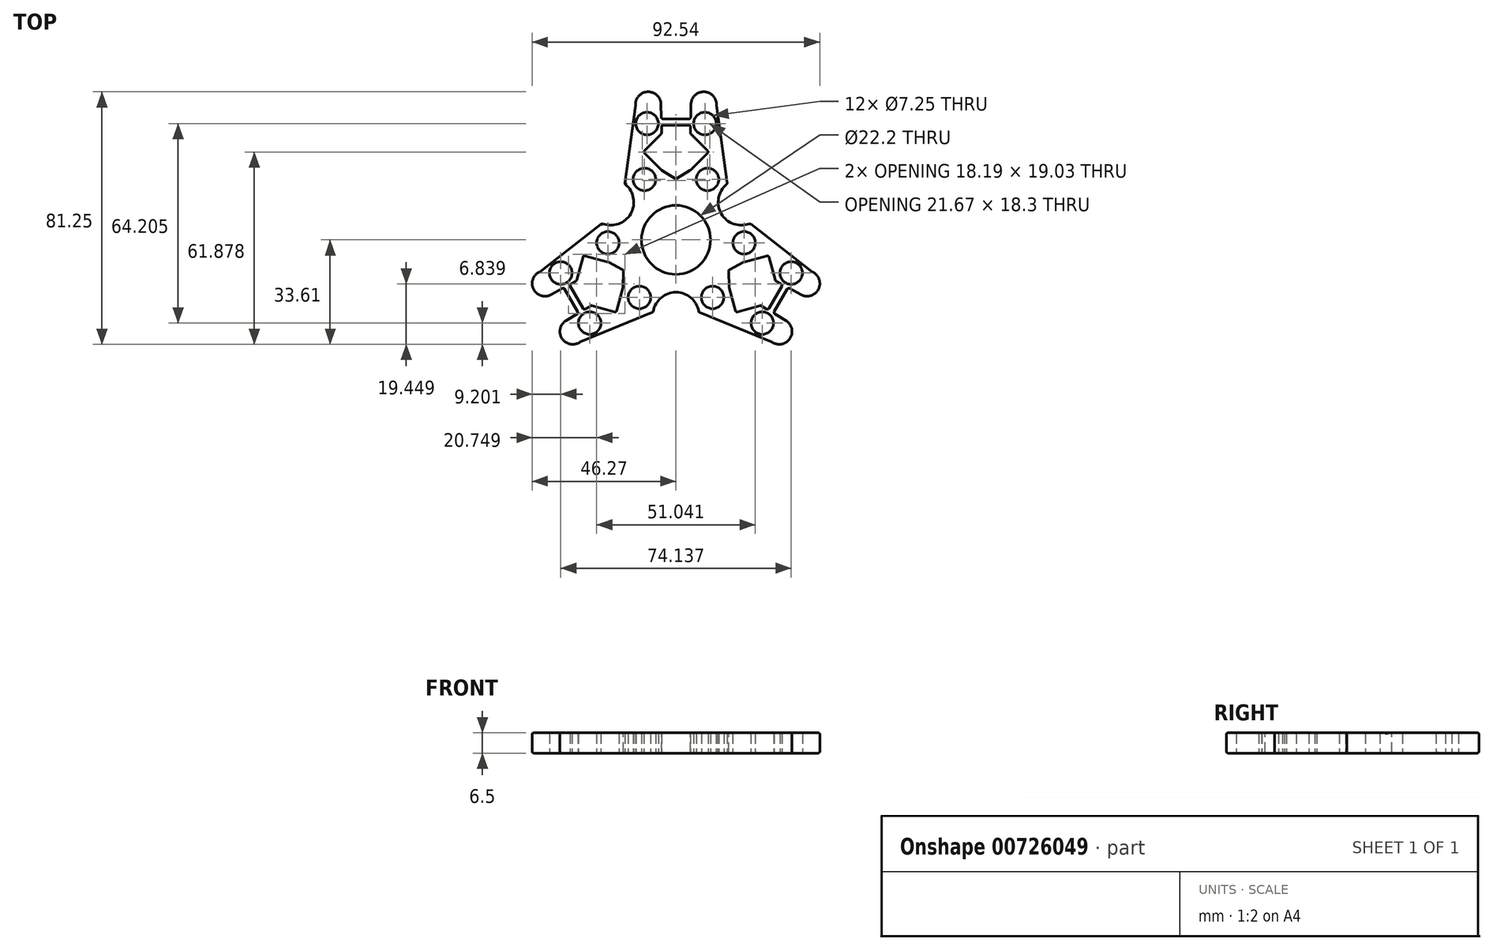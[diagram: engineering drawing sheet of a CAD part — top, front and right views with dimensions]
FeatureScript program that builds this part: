
annotation { "Feature Type Name" : "Feature", "Feature Type Description" : "" }
export const myFeature = defineFeature(function(context is Context, id is Id, definition is map)
    precondition{}
    {
        {
            var Q0;
            Q0=qCreatedBy(makeId("Top.planeOp"),FACE);
            var sketch = newSketch(context, id + "F0", { "sketchPlane" : qUnion([Q0])});
            skCircle(sketch, "E0", {"center": v(0, 0) * mm, "radius": 11.1 * mm});
            skCircle(sketch, "E1", {"center": v(0, 0) * mm, "radius": 14 * mm});
            skPoint(sketch, "E2", {"position": v(-16.47, 18) * mm});
            skPoint(sketch, "E3", {"position": v(-13.03, 43.23) * mm});
            skPoint(sketch, "E4.MirrorP", {"position": v(13.03, 43.23) * mm});
            skPoint(sketch, "E5.MirrorP", {"position": v(16.47, 18) * mm});
            skPoint(sketch, "E6", {"position": v(-4.8, 43.61) * mm});
            skPoint(sketch, "E7", {"position": v(-4.62, 34.25) * mm});
            skPoint(sketch, "E8", {"position": v(-10.54, 28.32) * mm});
            skPoint(sketch, "E9", {"position": v(-4.62, 22.4) * mm});
            skPoint(sketch, "E10", {"position": v(0, 19.53) * mm});
            skPoint(sketch, "E11.MirrorP", {"position": v(4.62, 22.4) * mm});
            skPoint(sketch, "E12.MirrorP", {"position": v(10.54, 28.32) * mm});
            skPoint(sketch, "E13.MirrorP", {"position": v(4.62, 34.25) * mm});
            skPoint(sketch, "E14.MirrorP", {"position": v(4.8, 43.61) * mm});
            skLineSegment(sketch, "E15", {"start": v(-16.47, 18) * mm, "end": v(-13.03, 43.23) * mm});
            skLineSegment(sketch, "E16", {"start": v(-13.03, 43.23) * mm, "end": v(-4.8, 43.61) * mm});
            skLineSegment(sketch, "E17", {"start": v(-4.8, 43.61) * mm, "end": v(-4.62, 34.25) * mm});
            skLineSegment(sketch, "E18", {"start": v(-10.54, 28.32) * mm, "end": v(-4.62, 34.25) * mm});
            skLineSegment(sketch, "E19", {"start": v(-10.54, 28.32) * mm, "end": v(-4.62, 22.4) * mm});
            skLineSegment(sketch, "E20", {"start": v(-4.62, 22.4) * mm, "end": v(0, 19.53) * mm});
            skLineSegment(sketch, "E21", {"start": v(0, 19.53) * mm, "end": v(4.62, 22.4) * mm});
            skLineSegment(sketch, "E22", {"start": v(4.62, 22.4) * mm, "end": v(10.54, 28.32) * mm});
            skLineSegment(sketch, "E23", {"start": v(4.62, 34.25) * mm, "end": v(10.54, 28.32) * mm});
            skLineSegment(sketch, "E24", {"start": v(4.62, 34.25) * mm, "end": v(4.8, 43.61) * mm});
            skLineSegment(sketch, "E25", {"start": v(13.03, 43.23) * mm, "end": v(4.8, 43.61) * mm});
            skLineSegment(sketch, "E26", {"start": v(13.03, 43.23) * mm, "end": v(16.47, 18) * mm});
            skPoint(sketch, "E27", {"position": v(-4.67, 36.92) * mm});
            skPoint(sketch, "E28", {"position": v(-4.71, 38.93) * mm});
            skPoint(sketch, "E29.MirrorP", {"position": v(4.67, 36.92) * mm});
            skPoint(sketch, "E30.MirrorP", {"position": v(4.71, 38.93) * mm});
            skCircle(sketch, "E31", {"center": v(-9.3, 37.43) * mm, "radius": 3.62 * mm});
            skCircle(sketch, "E32", {"center": v(-10.14, 19.45) * mm, "radius": 3.62 * mm});
            skCircle(sketch, "E33.MirrorC", {"center": v(10.14, 19.45) * mm, "radius": 3.62 * mm});
            skCircle(sketch, "E34.MirrorC", {"center": v(9.3, 37.43) * mm, "radius": 3.62 * mm});
            skLineSegment(sketch, "E35", {"start": v(-4.67, 36.92) * mm, "end": v(4.67, 36.92) * mm});
            skLineSegment(sketch, "E36", {"start": v(4.71, 38.93) * mm, "end": v(-4.71, 38.93) * mm});
            skArc(sketch, "E37", {"start": v(-4.8, 43.61) * mm, "mid": v(-9.12, 47.64) * mm, "end": v(-13.03, 43.23) * mm});
            skArc(sketch, "E38.MirrorCS", {"start": v(4.8, 43.61) * mm, "mid": v(9.12, 47.64) * mm, "end": v(13.03, 43.23) * mm});
            skArc(sketch, "E39.1.0", {"start": v(-35.36, -25.97) * mm, "mid": v(-36.7, -31.71) * mm, "end": v(-30.92, -32.9) * mm});
            skLineSegment(sketch, "E39.1.1", {"start": v(-30.92, -32.9) * mm, "end": v(-35.36, -25.97) * mm});
            skLineSegment(sketch, "E39.1.2", {"start": v(-35.36, -25.97) * mm, "end": v(-27.35, -21.12) * mm});
            skLineSegment(sketch, "E39.1.3", {"start": v(-7.35, -23.26) * mm, "end": v(-30.92, -32.9) * mm});
            skCircle(sketch, "E39.1.4", {"center": v(-27.77, -26.77) * mm, "radius": 3.62 * mm});
            skLineSegment(sketch, "E39.1.5", {"start": v(-36.07, -15.38) * mm, "end": v(-31.36, -23.55) * mm});
            skLineSegment(sketch, "E39.1.6", {"start": v(-29.64, -22.5) * mm, "end": v(-34.3, -14.41) * mm});
            skLineSegment(sketch, "E39.1.7", {"start": v(-31.97, -13.12) * mm, "end": v(-40.17, -17.64) * mm});
            skLineSegment(sketch, "E39.1.8", {"start": v(-43.95, -10.33) * mm, "end": v(-40.17, -17.64) * mm});
            skArc(sketch, "E39.1.9", {"start": v(-40.17, -17.64) * mm, "mid": v(-45.81, -15.93) * mm, "end": v(-43.95, -10.33) * mm});
            skLineSegment(sketch, "E39.1.10", {"start": v(-43.95, -10.33) * mm, "end": v(-23.82, 5.26) * mm});
            skCircle(sketch, "E39.1.11", {"center": v(-37.07, -10.66) * mm, "radius": 3.62 * mm});
            skLineSegment(sketch, "E39.1.12", {"start": v(-31.97, -13.12) * mm, "end": v(-29.8, -5.03) * mm});
            skLineSegment(sketch, "E39.1.13", {"start": v(-21.7, -7.2) * mm, "end": v(-29.8, -5.03) * mm});
            skArc(sketch, "E39.2.0", {"start": v(40.17, -17.64) * mm, "mid": v(45.81, -15.93) * mm, "end": v(43.95, -10.33) * mm});
            skLineSegment(sketch, "E39.2.1", {"start": v(43.95, -10.33) * mm, "end": v(40.17, -17.64) * mm});
            skLineSegment(sketch, "E39.2.2", {"start": v(40.17, -17.64) * mm, "end": v(31.97, -13.12) * mm});
            skLineSegment(sketch, "E39.2.3", {"start": v(23.82, 5.26) * mm, "end": v(43.95, -10.33) * mm});
            skCircle(sketch, "E39.2.4", {"center": v(37.07, -10.66) * mm, "radius": 3.62 * mm});
            skLineSegment(sketch, "E39.2.5", {"start": v(31.36, -23.55) * mm, "end": v(36.07, -15.38) * mm});
            skLineSegment(sketch, "E39.2.6", {"start": v(34.3, -14.41) * mm, "end": v(29.64, -22.5) * mm});
            skLineSegment(sketch, "E39.2.7", {"start": v(27.35, -21.12) * mm, "end": v(35.36, -25.97) * mm});
            skLineSegment(sketch, "E39.2.8", {"start": v(30.92, -32.9) * mm, "end": v(35.36, -25.97) * mm});
            skArc(sketch, "E39.2.9", {"start": v(35.36, -25.97) * mm, "mid": v(36.7, -31.71) * mm, "end": v(30.92, -32.9) * mm});
            skLineSegment(sketch, "E39.2.10", {"start": v(30.92, -32.9) * mm, "end": v(7.35, -23.26) * mm});
            skCircle(sketch, "E39.2.11", {"center": v(27.77, -26.77) * mm, "radius": 3.62 * mm});
            skLineSegment(sketch, "E39.2.12", {"start": v(27.35, -21.12) * mm, "end": v(19.26, -23.3) * mm});
            skLineSegment(sketch, "E39.2.13", {"start": v(17.09, -15.2) * mm, "end": v(19.26, -23.3) * mm});
            skLineSegment(sketch, "E40.1.0", {"start": v(-17.09, -15.2) * mm, "end": v(-16.91, -9.76) * mm});
            skLineSegment(sketch, "E40.1.1", {"start": v(-19.26, -23.3) * mm, "end": v(-17.09, -15.2) * mm});
            skLineSegment(sketch, "E40.1.2", {"start": v(-19.26, -23.3) * mm, "end": v(-27.35, -21.12) * mm});
            skCircle(sketch, "E40.1.7", {"center": v(-11.78, -18.51) * mm, "radius": 3.62 * mm});
            skCircle(sketch, "E40.1.10", {"center": v(-21.92, -0.94) * mm, "radius": 3.62 * mm});
            skLineSegment(sketch, "E40.2.0", {"start": v(21.7, -7.2) * mm, "end": v(16.91, -9.76) * mm});
            skLineSegment(sketch, "E40.2.1", {"start": v(29.8, -5.03) * mm, "end": v(21.7, -7.2) * mm});
            skLineSegment(sketch, "E40.2.2", {"start": v(29.8, -5.03) * mm, "end": v(31.97, -13.12) * mm});
            skCircle(sketch, "E40.2.7", {"center": v(21.92, -0.94) * mm, "radius": 3.62 * mm});
            skCircle(sketch, "E40.2.10", {"center": v(11.78, -18.51) * mm, "radius": 3.62 * mm});
            skArc(sketch, "E41", {"start": v(-23.82, 5.26) * mm, "mid": v(-14.58, 8.42) * mm, "end": v(-16.47, 18) * mm});
            skArc(sketch, "E42.1.0", {"start": v(7.35, -23.26) * mm, "mid": v(0, -16.83) * mm, "end": v(-7.35, -23.26) * mm});
            skArc(sketch, "E42.2.0", {"start": v(16.47, 18) * mm, "mid": v(14.58, 8.42) * mm, "end": v(23.82, 5.26) * mm});
            skLineSegment(sketch, "E43.1.1", {"start": v(-16.91, -9.76) * mm, "end": v(-21.7, -7.2) * mm});
            skLineSegment(sketch, "E43.2.1", {"start": v(16.91, -9.76) * mm, "end": v(17.09, -15.2) * mm});
            skSolve(sketch);
        }
        {
            var Q0;
            Q0=makeQuery(id+"F0.imprint","IMPRINT",FACE,{"disambiguationData":[TD([[makeQuery(id+"F0.imprint","IMPRINT",EDGE,{"derivedFrom":sQuery(id+"F0.wireOp",EDGE,"E1")}),-1.0]])]});
            var Q1;
            {var subQ0=sQuery(id+"F0.wireOp",EDGE,"E39.1.6");Q1=makeQuery(id+"F0.imprint","IMPRINT",FACE,{"disambiguationData":[TD([[makeQuery(id+"F0.imprint","IMPRINT",EDGE,{"derivedFrom":subQ0}),1.0]])]});}
            var Q2;
            Q2=makeQuery(id+"F0.imprint","IMPRINT",FACE,{"disambiguationData":[TD([[makeQuery(id+"F0.imprint","IMPRINT",EDGE,{"derivedFrom":sQuery(id+"F0.wireOp",EDGE,"E39.1.0")}),1.0]])]});
            var Q3;
            Q3=makeQuery(id+"F0.imprint","IMPRINT",FACE,{"disambiguationData":[TD([[makeQuery(id+"F0.imprint","IMPRINT",EDGE,{"derivedFrom":sQuery(id+"F0.wireOp",EDGE,"E39.1.8")}),-1.0]])]});
            var Q4;
            Q4=makeQuery(id+"F0.imprint","IMPRINT",FACE,{"disambiguationData":[TD([[makeQuery(id+"F0.imprint","IMPRINT",EDGE,{"derivedFrom":sQuery(id+"F0.wireOp",EDGE,"E16")}),1.0]])]});
            var Q5;
            {var subQ0=sQuery(id+"F0.wireOp",EDGE,"E35");Q5=makeQuery(id+"F0.imprint","IMPRINT",FACE,{"disambiguationData":[TD([[makeQuery(id+"F0.imprint","IMPRINT",EDGE,{"derivedFrom":subQ0}),1.0]])]});}
            var Q6;
            Q6=makeQuery(id+"F0.imprint","IMPRINT",FACE,{"disambiguationData":[TD([[makeQuery(id+"F0.imprint","IMPRINT",EDGE,{"derivedFrom":sQuery(id+"F0.wireOp",EDGE,"E25")}),-1.0]])]});
            var Q7;
            Q7=makeQuery(id+"F0.imprint","IMPRINT",FACE,{"disambiguationData":[TD([[makeQuery(id+"F0.imprint","IMPRINT",EDGE,{"derivedFrom":sQuery(id+"F0.wireOp",EDGE,"E39.2.0")}),1.0]])]});
            var Q8;
            Q8=makeQuery(id+"F0.imprint","IMPRINT",FACE,{"disambiguationData":[TD([[makeQuery(id+"F0.imprint","IMPRINT",EDGE,{"derivedFrom":sQuery(id+"F0.wireOp",EDGE,"E39.2.8")}),-1.0]])]});
            var Q9;
            {var subQ0=sQuery(id+"F0.wireOp",EDGE,"E39.2.6");Q9=makeQuery(id+"F0.imprint","IMPRINT",FACE,{"disambiguationData":[TD([[makeQuery(id+"F0.imprint","IMPRINT",EDGE,{"derivedFrom":subQ0}),1.0]])]});}
            var Q10;
            Q10=makeQuery(id+"F0.imprint","IMPRINT",FACE,{"disambiguationData":[TD([[makeQuery(id+"F0.imprint","IMPRINT",EDGE,{"derivedFrom":sQuery(id+"F0.wireOp",EDGE,"E0")}),-1.0]])]});
            extrude(context, id + "F1", {"entities" : qUnion([Q0, Q1, Q2, Q3, Q4, Q5, Q6, Q7, Q8, Q9, Q10]), "depth" : 6.5 * mm, "offsetDistance" : 25 * mm});
        }
        {
            var Q0;
            Q0=makeQuery(id+"F1.opExtrude","SWEPT_EDGE",EDGE,{"disambiguationData":[OSD([sQuery(id+"F0.wireOp",EDGE,"E40.1.1"),sQuery(id+"F0.wireOp",EDGE,"E40.1.0")])]});
            var Q1;
            Q1=makeQuery(id+"F1.opExtrude","SWEPT_FACE",FACE,{"disambiguationData":[OSD([sQuery(id+"F0.wireOp",EDGE,"E40.1.2")])]});
            var Q2;
            Q2=makeQuery(id+"F1.opExtrude","SWEPT_FACE",FACE,{"disambiguationData":[OSD([sQuery(id+"F0.wireOp",EDGE,"E39.2.0")])]});
            var Q3;
            Q3=makeQuery(id+"F1.opExtrude","SWEPT_EDGE",EDGE,{"disambiguationData":[OSD([sQuery(id+"F0.wireOp",EDGE,"E39.2.2"),sQuery(id+"F0.wireOp",EDGE,"E39.2.5")])]});
            var Q4;
            {var subQ0=sQuery(id+"F0.wireOp",EDGE,"E39.2.2");Q4=makeQuery(id+"F1.opExtrude","CAP_EDGE",EDGE,{"disambiguationData":[OSD([subQ0]),TDD([makeQuery(id+"F0.imprint","IMPRINT",EDGE,{"disambiguationData":[TD([[makeQuery(id+"F0.imprint","INTERSECT",VERTEX,{"derivedFrom":[sQuery(id+"F0.wireOp",EDGE,"E40.2.2"),subQ0]}),1.0]])],"derivedFrom":subQ0})])],"isStart":true});}
            var Q5;
            Q5=makeQuery(id+"F1.opExtrude","CAP_EDGE",EDGE,{"disambiguationData":[OSD([sQuery(id+"F0.wireOp",EDGE,"E19")])],"isStart":false});
            var Q6;
            Q6=makeQuery(id+"F1.opExtrude","SWEPT_FACE",FACE,{"disambiguationData":[OSD([sQuery(id+"F0.wireOp",EDGE,"E39.2.10")])]});
            var Q7;
            Q7=makeQuery(id+"F1.opExtrude","SWEPT_FACE",FACE,{"disambiguationData":[OSD([sQuery(id+"F0.wireOp",EDGE,"E32")])]});
            var Q8;
            Q8=makeQuery(id+"F1.opExtrude","SWEPT_FACE",FACE,{"disambiguationData":[OSD([sQuery(id+"F0.wireOp",EDGE,"E35")])]});
            var Q9;
            {var subQ0=sQuery(id+"F0.wireOp",EDGE,"E39.2.7");Q9=makeQuery(id+"F1.opExtrude","SWEPT_FACE",FACE,{"disambiguationData":[OSD([subQ0]),TDD([makeQuery(id+"F0.imprint","IMPRINT",EDGE,{"disambiguationData":[TD([[makeQuery(id+"F0.imprint","INTERSECT",VERTEX,{"derivedFrom":[subQ0,sQuery(id+"F0.wireOp",EDGE,"E39.2.5")]}),-1.0]])],"derivedFrom":subQ0})])]});}
            var Q10;
            Q10=makeQuery(id+"F1.opExtrude","SWEPT_FACE",FACE,{"disambiguationData":[OSD([sQuery(id+"F0.wireOp",EDGE,"E40.1.1")])]});
            var Q11;
            {var subQ0=sQuery(id+"F0.wireOp",EDGE,"E39.2.7");Q11=makeQuery(id+"F1.opExtrude","SWEPT_FACE",FACE,{"disambiguationData":[OSD([subQ0]),TDD([makeQuery(id+"F0.imprint","IMPRINT",EDGE,{"disambiguationData":[TD([[makeQuery(id+"F0.imprint","INTERSECT",VERTEX,{"derivedFrom":[sQuery(id+"F0.wireOp",EDGE,"E39.2.12"),subQ0]}),-1.0]])],"derivedFrom":subQ0})])]});}
            var Q12;
            Q12=makeQuery(id+"F1.opExtrude","CAP_EDGE",EDGE,{"disambiguationData":[OSD([sQuery(id+"F0.wireOp",EDGE,"E39.2.13")])],"isStart":false});
            var Q13;
            Q13=makeQuery(id+"F1.opExtrude","CAP_EDGE",EDGE,{"disambiguationData":[OSD([sQuery(id+"F0.wireOp",EDGE,"E39.2.12")])],"isStart":false});
            var Q14;
            Q14=makeQuery(id+"F1.opExtrude","SWEPT_FACE",FACE,{"disambiguationData":[OSD([sQuery(id+"F0.wireOp",EDGE,"E40.1.10")])]});
            var Q15;
            Q15=makeQuery(id+"F1.opExtrude","CAP_EDGE",EDGE,{"disambiguationData":[OSD([sQuery(id+"F0.wireOp",EDGE,"E39.1.5")])],"isStart":false});
            var Q16;
            Q16=makeQuery(id+"F1.opExtrude","SWEPT_FACE",FACE,{"disambiguationData":[OSD([sQuery(id+"F0.wireOp",EDGE,"E40.1.0")])]});
            var Q17;
            Q17=makeQuery(id+"F1.opExtrude","SWEPT_FACE",FACE,{"disambiguationData":[OSD([sQuery(id+"F0.wireOp",EDGE,"E39.2.3")])]});
            var Q18;
            Q18=makeQuery(id+"F1.opExtrude","CAP_EDGE",EDGE,{"disambiguationData":[OSD([sQuery(id+"F0.wireOp",EDGE,"E39.1.10")])],"isStart":false});
            var Q19;
            Q19=makeQuery(id+"F1.opExtrude","CAP_EDGE",EDGE,{"disambiguationData":[OSD([sQuery(id+"F0.wireOp",EDGE,"E22")])],"isStart":false});
            var Q20;
            Q20=makeQuery(id+"F1.opExtrude","CAP_EDGE",EDGE,{"disambiguationData":[OSD([sQuery(id+"F0.wireOp",EDGE,"E40.2.0")])],"isStart":false});
            var Q21;
            Q21=makeQuery(id+"F1.opExtrude","SWEPT_FACE",FACE,{"disambiguationData":[OSD([sQuery(id+"F0.wireOp",EDGE,"E39.1.11")])]});
            var Q22;
            Q22=makeQuery(id+"F1.opExtrude","CAP_EDGE",EDGE,{"disambiguationData":[OSD([sQuery(id+"F0.wireOp",EDGE,"E39.1.3")])],"isStart":true});
            var Q23;
            Q23=makeQuery(id+"F1.opExtrude","CAP_EDGE",EDGE,{"disambiguationData":[OSD([sQuery(id+"F0.wireOp",EDGE,"E39.1.5")])],"isStart":true});
            var Q24;
            Q24=makeQuery(id+"F1.opExtrude","SWEPT_FACE",FACE,{"disambiguationData":[OSD([sQuery(id+"F0.wireOp",EDGE,"E42.2.0")])]});
            var Q25;
            Q25=makeQuery(id+"F1.opExtrude","CAP_EDGE",EDGE,{"disambiguationData":[OSD([sQuery(id+"F0.wireOp",EDGE,"E0")])],"isStart":false});
            var Q26;
            Q26=makeQuery(id+"F1.opExtrude","CAP_EDGE",EDGE,{"disambiguationData":[OSD([sQuery(id+"F0.wireOp",EDGE,"E0")])],"isStart":true});
            var Q27;
            Q27=makeQuery(id+"F1.opExtrude","CAP_EDGE",EDGE,{"disambiguationData":[OSD([sQuery(id+"F0.wireOp",EDGE,"E39.2.10")])],"isStart":false});
            var Q28;
            Q28=makeQuery(id+"F1.opExtrude","CAP_EDGE",EDGE,{"disambiguationData":[OSD([sQuery(id+"F0.wireOp",EDGE,"E39.1.6")])],"isStart":false});
            var Q29;
            Q29=makeQuery(id+"F1.opExtrude","CAP_EDGE",EDGE,{"disambiguationData":[OSD([sQuery(id+"F0.wireOp",EDGE,"E40.2.2")])],"isStart":false});
            var Q30;
            Q30=makeQuery(id+"F1.opExtrude","SWEPT_FACE",FACE,{"disambiguationData":[OSD([sQuery(id+"F0.wireOp",EDGE,"E39.2.9")])]});
            var Q31;
            Q31=makeQuery(id+"F1.opExtrude","SWEPT_FACE",FACE,{"disambiguationData":[OSD([sQuery(id+"F0.wireOp",EDGE,"E40.2.1")])]});
            var Q32;
            {var subQ0=sQuery(id+"F0.wireOp",EDGE,"E24");Q32=makeQuery(id+"F1.opExtrude","SWEPT_FACE",FACE,{"disambiguationData":[OSD([subQ0]),TDD([makeQuery(id+"F0.imprint","IMPRINT",EDGE,{"disambiguationData":[TD([[makeQuery(id+"F0.imprint","INTERSECT",VERTEX,{"derivedFrom":[sQuery(id+"F0.wireOp",EDGE,"E23"),subQ0]}),-1.0]])],"derivedFrom":subQ0})])]});}
            var Q33;
            Q33=makeQuery(id+"F1.opExtrude","SWEPT_FACE",FACE,{"disambiguationData":[OSD([sQuery(id+"F0.wireOp",EDGE,"E23")])]});
            var Q34;
            Q34=makeQuery(id+"F1.opExtrude","SWEPT_FACE",FACE,{"disambiguationData":[OSD([sQuery(id+"F0.wireOp",EDGE,"E43.2.1")])]});
            var Q35;
            {var subQ0=sQuery(id+"F0.wireOp",EDGE,"E39.2.2");Q35=makeQuery(id+"F1.opExtrude","SWEPT_FACE",FACE,{"disambiguationData":[OSD([subQ0]),TDD([makeQuery(id+"F0.imprint","IMPRINT",EDGE,{"disambiguationData":[TD([[makeQuery(id+"F0.imprint","INTERSECT",VERTEX,{"derivedFrom":[subQ0,sQuery(id+"F0.wireOp",EDGE,"E39.2.5")]}),1.0]])],"derivedFrom":subQ0})])]});}
            var Q36;
            Q36=makeQuery(id+"F1.opExtrude","SWEPT_FACE",FACE,{"disambiguationData":[OSD([sQuery(id+"F0.wireOp",EDGE,"E33.MirrorC")])]});
            var Q37;
            Q37=makeQuery(id+"F1.opExtrude","SWEPT_FACE",FACE,{"disambiguationData":[OSD([sQuery(id+"F0.wireOp",EDGE,"E39.2.13")])]});
            var Q38;
            Q38=makeQuery(id+"F1.opExtrude","CAP_EDGE",EDGE,{"disambiguationData":[OSD([sQuery(id+"F0.wireOp",EDGE,"E39.2.10")])],"isStart":true});
            var Q39;
            Q39=makeQuery(id+"F1.opExtrude","SWEPT_FACE",FACE,{"disambiguationData":[OSD([sQuery(id+"F0.wireOp",EDGE,"E22")])]});
            var Q40;
            Q40=makeQuery(id+"F1.opExtrude","SWEPT_FACE",FACE,{"disambiguationData":[OSD([sQuery(id+"F0.wireOp",EDGE,"E21")])]});
            var Q41;
            Q41=makeQuery(id+"F1.opExtrude","SWEPT_EDGE",EDGE,{"disambiguationData":[OSD([sQuery(id+"F0.wireOp",EDGE,"E23"),sQuery(id+"F0.wireOp",EDGE,"E24")])]});
            var Q42;
            {var subQ0=sQuery(id+"F0.wireOp",EDGE,"E39.2.2");Q42=makeQuery(id+"F1.opExtrude","SWEPT_FACE",FACE,{"disambiguationData":[OSD([subQ0]),TDD([makeQuery(id+"F0.imprint","IMPRINT",EDGE,{"disambiguationData":[TD([[makeQuery(id+"F0.imprint","INTERSECT",VERTEX,{"derivedFrom":[sQuery(id+"F0.wireOp",EDGE,"E40.2.2"),subQ0]}),1.0]])],"derivedFrom":subQ0})])]});}
            var Q43;
            Q43=makeQuery(id+"F1.opExtrude","SWEPT_FACE",FACE,{"disambiguationData":[OSD([sQuery(id+"F0.wireOp",EDGE,"E34.MirrorC")])]});
            var Q44;
            Q44=makeQuery(id+"F1.opExtrude","SWEPT_FACE",FACE,{"disambiguationData":[OSD([sQuery(id+"F0.wireOp",EDGE,"E43.1.1")])]});
            var Q45;
            Q45=makeQuery(id+"F1.opExtrude","SWEPT_FACE",FACE,{"disambiguationData":[OSD([sQuery(id+"F0.wireOp",EDGE,"E20")])]});
            var Q46;
            Q46=makeQuery(id+"F1.opExtrude","CAP_EDGE",EDGE,{"disambiguationData":[OSD([sQuery(id+"F0.wireOp",EDGE,"E39.1.9")])],"isStart":true});
            var Q47;
            Q47=makeQuery(id+"F1.opExtrude","SWEPT_EDGE",EDGE,{"disambiguationData":[OSD([sQuery(id+"F0.wireOp",EDGE,"E40.1.0"),sQuery(id+"F0.wireOp",EDGE,"E43.1.1")])]});
            var Q48;
            Q48=makeQuery(id+"F1.opExtrude","SWEPT_FACE",FACE,{"disambiguationData":[OSD([sQuery(id+"F0.wireOp",EDGE,"E19")])]});
            var Q49;
            Q49=makeQuery(id+"F1.opExtrude","SWEPT_FACE",FACE,{"disambiguationData":[OSD([sQuery(id+"F0.wireOp",EDGE,"E18")])]});
            var Q50;
            {var subQ0=sQuery(id+"F0.wireOp",EDGE,"E17");Q50=makeQuery(id+"F1.opExtrude","SWEPT_FACE",FACE,{"disambiguationData":[OSD([subQ0]),TDD([makeQuery(id+"F0.imprint","IMPRINT",EDGE,{"disambiguationData":[TD([[makeQuery(id+"F0.imprint","INTERSECT",VERTEX,{"derivedFrom":[subQ0,sQuery(id+"F0.wireOp",EDGE,"E18")]}),1.0]])],"derivedFrom":subQ0})])]});}
            var Q51;
            Q51=makeQuery(id+"F1.opExtrude","SWEPT_FACE",FACE,{"disambiguationData":[OSD([sQuery(id+"F0.wireOp",EDGE,"E40.2.0")])]});
            var Q52;
            Q52=makeQuery(id+"F1.opExtrude","SWEPT_FACE",FACE,{"disambiguationData":[OSD([sQuery(id+"F0.wireOp",EDGE,"E40.2.2")])]});
            var Q53;
            {var subQ0=sQuery(id+"F0.wireOp",EDGE,"E17");Q53=makeQuery(id+"F1.opExtrude","SWEPT_FACE",FACE,{"disambiguationData":[OSD([subQ0]),TDD([makeQuery(id+"F0.imprint","IMPRINT",EDGE,{"disambiguationData":[TD([[makeQuery(id+"F0.imprint","INTERSECT",VERTEX,{"derivedFrom":[subQ0,sQuery(id+"F0.wireOp",EDGE,"E36")]}),1.0]])],"derivedFrom":subQ0})])]});}
            var Q54;
            Q54=makeQuery(id+"F1.opExtrude","SWEPT_EDGE",EDGE,{"disambiguationData":[OSD([sQuery(id+"F0.wireOp",EDGE,"E17"),sQuery(id+"F0.wireOp",EDGE,"E18")])]});
            var Q55;
            Q55=makeQuery(id+"F1.opExtrude","CAP_FACE",FACE,{"disambiguationData":[OSD([sQuery(id+"F0.wireOp",EDGE,"E0"),sQuery(id+"F0.wireOp",EDGE,"E15"),sQuery(id+"F0.wireOp",EDGE,"E17"),sQuery(id+"F0.wireOp",EDGE,"E18"),sQuery(id+"F0.wireOp",EDGE,"E19"),sQuery(id+"F0.wireOp",EDGE,"E20"),sQuery(id+"F0.wireOp",EDGE,"E21"),sQuery(id+"F0.wireOp",EDGE,"E22"),sQuery(id+"F0.wireOp",EDGE,"E23"),sQuery(id+"F0.wireOp",EDGE,"E24"),sQuery(id+"F0.wireOp",EDGE,"E26"),sQuery(id+"F0.wireOp",EDGE,"E31"),sQuery(id+"F0.wireOp",EDGE,"E32"),sQuery(id+"F0.wireOp",EDGE,"E33.MirrorC"),sQuery(id+"F0.wireOp",EDGE,"E34.MirrorC"),sQuery(id+"F0.wireOp",EDGE,"E35"),sQuery(id+"F0.wireOp",EDGE,"E36"),sQuery(id+"F0.wireOp",EDGE,"E37"),sQuery(id+"F0.wireOp",EDGE,"E38.MirrorCS"),sQuery(id+"F0.wireOp",EDGE,"E39.1.0"),sQuery(id+"F0.wireOp",EDGE,"E39.1.3"),sQuery(id+"F0.wireOp",EDGE,"E39.1.9"),sQuery(id+"F0.wireOp",EDGE,"E39.1.10"),sQuery(id+"F0.wireOp",EDGE,"E39.1.12"),sQuery(id+"F0.wireOp",EDGE,"E39.1.13"),sQuery(id+"F0.wireOp",EDGE,"E39.2.0"),sQuery(id+"F0.wireOp",EDGE,"E39.2.3"),sQuery(id+"F0.wireOp",EDGE,"E39.2.9"),sQuery(id+"F0.wireOp",EDGE,"E39.2.10"),sQuery(id+"F0.wireOp",EDGE,"E39.2.12"),sQuery(id+"F0.wireOp",EDGE,"E39.2.13"),sQuery(id+"F0.wireOp",EDGE,"E40.1.1"),sQuery(id+"F0.wireOp",EDGE,"E40.1.2"),sQuery(id+"F0.wireOp",EDGE,"E39.1.2"),sQuery(id+"F0.wireOp",EDGE,"E39.1.7"),sQuery(id+"F0.wireOp",EDGE,"E39.1.6"),sQuery(id+"F0.wireOp",EDGE,"E39.1.5"),sQuery(id+"F0.wireOp",EDGE,"E40.1.7"),sQuery(id+"F0.wireOp",EDGE,"E39.1.4"),sQuery(id+"F0.wireOp",EDGE,"E39.1.11"),sQuery(id+"F0.wireOp",EDGE,"E40.1.10"),sQuery(id+"F0.wireOp",EDGE,"E40.2.1"),sQuery(id+"F0.wireOp",EDGE,"E40.2.2"),sQuery(id+"F0.wireOp",EDGE,"E39.2.2"),sQuery(id+"F0.wireOp",EDGE,"E39.2.7"),sQuery(id+"F0.wireOp",EDGE,"E39.2.6"),sQuery(id+"F0.wireOp",EDGE,"E39.2.5"),sQuery(id+"F0.wireOp",EDGE,"E40.2.7"),sQuery(id+"F0.wireOp",EDGE,"E39.2.4"),sQuery(id+"F0.wireOp",EDGE,"E39.2.11"),sQuery(id+"F0.wireOp",EDGE,"E40.2.10"),sQuery(id+"F0.wireOp",EDGE,"E41"),sQuery(id+"F0.wireOp",EDGE,"E42.1.0"),sQuery(id+"F0.wireOp",EDGE,"E42.2.0"),sQuery(id+"F0.wireOp",EDGE,"E40.1.0"),sQuery(id+"F0.wireOp",EDGE,"E43.1.1"),sQuery(id+"F0.wireOp",EDGE,"E40.2.0"),sQuery(id+"F0.wireOp",EDGE,"E43.2.1")])],"isStart":false});
            var Q56;
            Q56=makeQuery(id+"F1.opExtrude","SWEPT_FACE",FACE,{"disambiguationData":[OSD([sQuery(id+"F0.wireOp",EDGE,"E15")])]});
            var Q57;
            Q57=makeQuery(id+"F1.opExtrude","CAP_EDGE",EDGE,{"disambiguationData":[OSD([sQuery(id+"F0.wireOp",EDGE,"E23")])],"isStart":true});
            var Q58;
            Q58=makeQuery(id+"F1.opExtrude","CAP_EDGE",EDGE,{"disambiguationData":[OSD([sQuery(id+"F0.wireOp",EDGE,"E35")])],"isStart":true});
            var Q59;
            Q59=makeQuery(id+"F1.opExtrude","CAP_EDGE",EDGE,{"disambiguationData":[OSD([sQuery(id+"F0.wireOp",EDGE,"E41")])],"isStart":true});
            var Q60;
            Q60=makeQuery(id+"F1.opExtrude","SWEPT_FACE",FACE,{"disambiguationData":[OSD([sQuery(id+"F0.wireOp",EDGE,"E37")])]});
            var Q61;
            {var subQ0=sQuery(id+"F0.wireOp",EDGE,"E39.1.2");Q61=makeQuery(id+"F1.opExtrude","SWEPT_FACE",FACE,{"disambiguationData":[OSD([subQ0]),TDD([makeQuery(id+"F0.imprint","IMPRINT",EDGE,{"disambiguationData":[TD([[makeQuery(id+"F0.imprint","INTERSECT",VERTEX,{"derivedFrom":[subQ0,sQuery(id+"F0.wireOp",EDGE,"E39.1.5")]}),1.0]])],"derivedFrom":subQ0})])]});}
            var Q62;
            Q62=makeQuery(id+"F1.opExtrude","SWEPT_FACE",FACE,{"disambiguationData":[OSD([sQuery(id+"F0.wireOp",EDGE,"E39.2.6")])]});
            var Q63;
            Q63=makeQuery(id+"F1.opExtrude","CAP_EDGE",EDGE,{"disambiguationData":[OSD([sQuery(id+"F0.wireOp",EDGE,"E23")])],"isStart":false});
            var Q64;
            Q64=makeQuery(id+"F1.opExtrude","CAP_EDGE",EDGE,{"disambiguationData":[OSD([sQuery(id+"F0.wireOp",EDGE,"E35")])],"isStart":false});
            var Q65;
            Q65=makeQuery(id+"F1.opExtrude","CAP_EDGE",EDGE,{"disambiguationData":[OSD([sQuery(id+"F0.wireOp",EDGE,"E41")])],"isStart":false});
            var Q66;
            Q66=makeQuery(id+"F1.opExtrude","SWEPT_FACE",FACE,{"disambiguationData":[OSD([sQuery(id+"F0.wireOp",EDGE,"E38.MirrorCS")])]});
            var Q67;
            {var subQ0=sQuery(id+"F0.wireOp",EDGE,"E39.1.2");Q67=makeQuery(id+"F1.opExtrude","SWEPT_FACE",FACE,{"disambiguationData":[OSD([subQ0]),TDD([makeQuery(id+"F0.imprint","IMPRINT",EDGE,{"disambiguationData":[TD([[makeQuery(id+"F0.imprint","INTERSECT",VERTEX,{"derivedFrom":[sQuery(id+"F0.wireOp",EDGE,"E40.1.2"),subQ0]}),1.0]])],"derivedFrom":subQ0})])]});}
            var Q68;
            Q68=makeQuery(id+"F1.opExtrude","SWEPT_FACE",FACE,{"disambiguationData":[OSD([sQuery(id+"F0.wireOp",EDGE,"E39.2.5")])]});
            var Q69;
            Q69=makeQuery(id+"F1.opExtrude","SWEPT_EDGE",EDGE,{"disambiguationData":[OSD([sQuery(id+"F0.wireOp",EDGE,"E39.1.12"),sQuery(id+"F0.wireOp",EDGE,"E39.1.7")])]});
            var Q70;
            Q70=makeQuery(id+"F1.opExtrude","CAP_EDGE",EDGE,{"disambiguationData":[OSD([sQuery(id+"F0.wireOp",EDGE,"E42.1.0")])],"isStart":true});
            var Q71;
            Q71=makeQuery(id+"F1.opExtrude","SWEPT_FACE",FACE,{"disambiguationData":[OSD([sQuery(id+"F0.wireOp",EDGE,"E39.1.0")])]});
            var Q72;
            {var subQ0=sQuery(id+"F0.wireOp",EDGE,"E39.1.7");Q72=makeQuery(id+"F1.opExtrude","SWEPT_FACE",FACE,{"disambiguationData":[OSD([subQ0]),TDD([makeQuery(id+"F0.imprint","IMPRINT",EDGE,{"disambiguationData":[TD([[makeQuery(id+"F0.imprint","INTERSECT",VERTEX,{"derivedFrom":[sQuery(id+"F0.wireOp",EDGE,"E39.1.12"),subQ0]}),-1.0]])],"derivedFrom":subQ0})])]});}
            var Q73;
            Q73=makeQuery(id+"F1.opExtrude","SWEPT_FACE",FACE,{"disambiguationData":[OSD([sQuery(id+"F0.wireOp",EDGE,"E40.2.7")])]});
            var Q74;
            Q74=makeQuery(id+"F1.opExtrude","SWEPT_EDGE",EDGE,{"disambiguationData":[OSD([sQuery(id+"F0.wireOp",EDGE,"E39.1.7"),sQuery(id+"F0.wireOp",EDGE,"E39.1.5")])]});
            var Q75;
            Q75=makeQuery(id+"F1.opExtrude","CAP_FACE",FACE,{"disambiguationData":[OSD([sQuery(id+"F0.wireOp",EDGE,"E0"),sQuery(id+"F0.wireOp",EDGE,"E15"),sQuery(id+"F0.wireOp",EDGE,"E17"),sQuery(id+"F0.wireOp",EDGE,"E18"),sQuery(id+"F0.wireOp",EDGE,"E19"),sQuery(id+"F0.wireOp",EDGE,"E20"),sQuery(id+"F0.wireOp",EDGE,"E21"),sQuery(id+"F0.wireOp",EDGE,"E22"),sQuery(id+"F0.wireOp",EDGE,"E23"),sQuery(id+"F0.wireOp",EDGE,"E24"),sQuery(id+"F0.wireOp",EDGE,"E26"),sQuery(id+"F0.wireOp",EDGE,"E31"),sQuery(id+"F0.wireOp",EDGE,"E32"),sQuery(id+"F0.wireOp",EDGE,"E33.MirrorC"),sQuery(id+"F0.wireOp",EDGE,"E34.MirrorC"),sQuery(id+"F0.wireOp",EDGE,"E35"),sQuery(id+"F0.wireOp",EDGE,"E36"),sQuery(id+"F0.wireOp",EDGE,"E37"),sQuery(id+"F0.wireOp",EDGE,"E38.MirrorCS"),sQuery(id+"F0.wireOp",EDGE,"E39.1.0"),sQuery(id+"F0.wireOp",EDGE,"E39.1.3"),sQuery(id+"F0.wireOp",EDGE,"E39.1.9"),sQuery(id+"F0.wireOp",EDGE,"E39.1.10"),sQuery(id+"F0.wireOp",EDGE,"E39.1.12"),sQuery(id+"F0.wireOp",EDGE,"E39.1.13"),sQuery(id+"F0.wireOp",EDGE,"E39.2.0"),sQuery(id+"F0.wireOp",EDGE,"E39.2.3"),sQuery(id+"F0.wireOp",EDGE,"E39.2.9"),sQuery(id+"F0.wireOp",EDGE,"E39.2.10"),sQuery(id+"F0.wireOp",EDGE,"E39.2.12"),sQuery(id+"F0.wireOp",EDGE,"E39.2.13"),sQuery(id+"F0.wireOp",EDGE,"E40.1.1"),sQuery(id+"F0.wireOp",EDGE,"E40.1.2"),sQuery(id+"F0.wireOp",EDGE,"E39.1.2"),sQuery(id+"F0.wireOp",EDGE,"E39.1.7"),sQuery(id+"F0.wireOp",EDGE,"E39.1.6"),sQuery(id+"F0.wireOp",EDGE,"E39.1.5"),sQuery(id+"F0.wireOp",EDGE,"E40.1.7"),sQuery(id+"F0.wireOp",EDGE,"E39.1.4"),sQuery(id+"F0.wireOp",EDGE,"E39.1.11"),sQuery(id+"F0.wireOp",EDGE,"E40.1.10"),sQuery(id+"F0.wireOp",EDGE,"E40.2.1"),sQuery(id+"F0.wireOp",EDGE,"E40.2.2"),sQuery(id+"F0.wireOp",EDGE,"E39.2.2"),sQuery(id+"F0.wireOp",EDGE,"E39.2.7"),sQuery(id+"F0.wireOp",EDGE,"E39.2.6"),sQuery(id+"F0.wireOp",EDGE,"E39.2.5"),sQuery(id+"F0.wireOp",EDGE,"E40.2.7"),sQuery(id+"F0.wireOp",EDGE,"E39.2.4"),sQuery(id+"F0.wireOp",EDGE,"E39.2.11"),sQuery(id+"F0.wireOp",EDGE,"E40.2.10"),sQuery(id+"F0.wireOp",EDGE,"E41"),sQuery(id+"F0.wireOp",EDGE,"E42.1.0"),sQuery(id+"F0.wireOp",EDGE,"E42.2.0"),sQuery(id+"F0.wireOp",EDGE,"E40.1.0"),sQuery(id+"F0.wireOp",EDGE,"E43.1.1"),sQuery(id+"F0.wireOp",EDGE,"E40.2.0"),sQuery(id+"F0.wireOp",EDGE,"E43.2.1")])],"isStart":true});
            var Q76;
            Q76=makeQuery(id+"F1.opExtrude","CAP_EDGE",EDGE,{"disambiguationData":[OSD([sQuery(id+"F0.wireOp",EDGE,"E36")])],"isStart":false});
            var Q77;
            Q77=makeQuery(id+"F1.opExtrude","CAP_EDGE",EDGE,{"disambiguationData":[OSD([sQuery(id+"F0.wireOp",EDGE,"E42.1.0")])],"isStart":false});
            var Q78;
            Q78=makeQuery(id+"F1.opExtrude","SWEPT_FACE",FACE,{"disambiguationData":[OSD([sQuery(id+"F0.wireOp",EDGE,"E39.1.3")])]});
            var Q79;
            {var subQ0=sQuery(id+"F0.wireOp",EDGE,"E39.1.7");Q79=makeQuery(id+"F1.opExtrude","SWEPT_FACE",FACE,{"disambiguationData":[OSD([subQ0]),TDD([makeQuery(id+"F0.imprint","IMPRINT",EDGE,{"disambiguationData":[TD([[makeQuery(id+"F0.imprint","INTERSECT",VERTEX,{"derivedFrom":[subQ0,sQuery(id+"F0.wireOp",EDGE,"E39.1.5")]}),-1.0]])],"derivedFrom":subQ0})])]});}
            var Q80;
            Q80=makeQuery(id+"F1.opExtrude","SWEPT_FACE",FACE,{"disambiguationData":[OSD([sQuery(id+"F0.wireOp",EDGE,"E39.2.4")])]});
            var Q81;
            Q81=makeQuery(id+"F1.opExtrude","SWEPT_FACE",FACE,{"disambiguationData":[OSD([sQuery(id+"F0.wireOp",EDGE,"E0")])]});
            var Q82;
            Q82=makeQuery(id+"F1.opExtrude","SWEPT_FACE",FACE,{"disambiguationData":[OSD([sQuery(id+"F0.wireOp",EDGE,"E26")])]});
            var Q83;
            {var subQ0=sQuery(id+"F0.wireOp",EDGE,"E24");Q83=makeQuery(id+"F1.opExtrude","SWEPT_FACE",FACE,{"disambiguationData":[OSD([subQ0]),TDD([makeQuery(id+"F0.imprint","IMPRINT",EDGE,{"disambiguationData":[TD([[makeQuery(id+"F0.imprint","INTERSECT",VERTEX,{"derivedFrom":[subQ0,sQuery(id+"F0.wireOp",EDGE,"E36")]}),-1.0]])],"derivedFrom":subQ0})])]});}
            var Q84;
            Q84=makeQuery(id+"F1.opExtrude","SWEPT_FACE",FACE,{"disambiguationData":[OSD([sQuery(id+"F0.wireOp",EDGE,"E31")])]});
            var Q85;
            Q85=makeQuery(id+"F1.opExtrude","SWEPT_EDGE",EDGE,{"disambiguationData":[OSD([sQuery(id+"F0.wireOp",EDGE,"E39.1.13"),sQuery(id+"F0.wireOp",EDGE,"E43.1.1")])]});
            var Q86;
            Q86=makeQuery(id+"F1.opExtrude","SWEPT_FACE",FACE,{"disambiguationData":[OSD([sQuery(id+"F0.wireOp",EDGE,"E39.1.9")])]});
            var Q87;
            Q87=makeQuery(id+"F1.opExtrude","SWEPT_FACE",FACE,{"disambiguationData":[OSD([sQuery(id+"F0.wireOp",EDGE,"E39.1.6")])]});
            var Q88;
            Q88=makeQuery(id+"F1.opExtrude","SWEPT_FACE",FACE,{"disambiguationData":[OSD([sQuery(id+"F0.wireOp",EDGE,"E39.2.11")])]});
            var Q89;
            Q89=makeQuery(id+"F1.opExtrude","SWEPT_EDGE",EDGE,{"disambiguationData":[OSD([sQuery(id+"F0.wireOp",EDGE,"E40.2.1"),sQuery(id+"F0.wireOp",EDGE,"E40.2.2")])]});
            var Q90;
            {var subQ0=sQuery(id+"F0.wireOp",EDGE,"E39.1.2");Q90=makeQuery(id+"F1.opExtrude","CAP_EDGE",EDGE,{"disambiguationData":[OSD([subQ0]),TDD([makeQuery(id+"F0.imprint","IMPRINT",EDGE,{"disambiguationData":[TD([[makeQuery(id+"F0.imprint","INTERSECT",VERTEX,{"derivedFrom":[subQ0,sQuery(id+"F0.wireOp",EDGE,"E39.1.5")]}),1.0]])],"derivedFrom":subQ0})])],"isStart":false});}
            var Q91;
            Q91=makeQuery(id+"F1.opExtrude","CAP_EDGE",EDGE,{"disambiguationData":[OSD([sQuery(id+"F0.wireOp",EDGE,"E42.2.0")])],"isStart":false});
            var Q92;
            Q92=makeQuery(id+"F1.opExtrude","SWEPT_FACE",FACE,{"disambiguationData":[OSD([sQuery(id+"F0.wireOp",EDGE,"E39.1.10")])]});
            var Q93;
            Q93=makeQuery(id+"F1.opExtrude","SWEPT_FACE",FACE,{"disambiguationData":[OSD([sQuery(id+"F0.wireOp",EDGE,"E39.1.5")])]});
            var Q94;
            Q94=makeQuery(id+"F1.opExtrude","SWEPT_FACE",FACE,{"disambiguationData":[OSD([sQuery(id+"F0.wireOp",EDGE,"E40.2.10")])]});
            var Q95;
            Q95=makeQuery(id+"F1.opExtrude","SWEPT_EDGE",EDGE,{"disambiguationData":[OSD([sQuery(id+"F0.wireOp",EDGE,"E40.2.1"),sQuery(id+"F0.wireOp",EDGE,"E40.2.0")])]});
            var Q96;
            Q96=makeQuery(id+"F1.opExtrude","SWEPT_FACE",FACE,{"disambiguationData":[OSD([sQuery(id+"F0.wireOp",EDGE,"E39.1.12")])]});
            var Q97;
            Q97=makeQuery(id+"F1.opExtrude","SWEPT_FACE",FACE,{"disambiguationData":[OSD([sQuery(id+"F0.wireOp",EDGE,"E40.1.7")])]});
            var Q98;
            Q98=makeQuery(id+"F1.opExtrude","SWEPT_FACE",FACE,{"disambiguationData":[OSD([sQuery(id+"F0.wireOp",EDGE,"E41")])]});
            var Q99;
            Q99=makeQuery(id+"F1.opExtrude","SWEPT_EDGE",EDGE,{"disambiguationData":[OSD([sQuery(id+"F0.wireOp",EDGE,"E40.2.2"),sQuery(id+"F0.wireOp",EDGE,"E39.2.2")])]});
            var Q100;
            Q100=makeQuery(id+"F1.opExtrude","CAP_EDGE",EDGE,{"disambiguationData":[OSD([sQuery(id+"F0.wireOp",EDGE,"E18")])],"isStart":false});
            var Q101;
            Q101=makeQuery(id+"F1.opExtrude","CAP_EDGE",EDGE,{"disambiguationData":[OSD([sQuery(id+"F0.wireOp",EDGE,"E26")])],"isStart":false});
            var Q102;
            Q102=makeQuery(id+"F1.opExtrude","CAP_EDGE",EDGE,{"disambiguationData":[OSD([sQuery(id+"F0.wireOp",EDGE,"E39.2.3")])],"isStart":false});
            var Q103;
            Q103=makeQuery(id+"F1.opExtrude","SWEPT_FACE",FACE,{"disambiguationData":[OSD([sQuery(id+"F0.wireOp",EDGE,"E39.1.13")])]});
            var Q104;
            Q104=makeQuery(id+"F1.opExtrude","SWEPT_FACE",FACE,{"disambiguationData":[OSD([sQuery(id+"F0.wireOp",EDGE,"E39.1.4")])]});
            var Q105;
            Q105=makeQuery(id+"F1.opExtrude","SWEPT_FACE",FACE,{"disambiguationData":[OSD([sQuery(id+"F0.wireOp",EDGE,"E42.1.0")])]});
            var Q106;
            Q106=makeQuery(id+"F1.opExtrude","CAP_EDGE",EDGE,{"disambiguationData":[OSD([sQuery(id+"F0.wireOp",EDGE,"E39.1.9")])],"isStart":false});
            var Q107;
            Q107=makeQuery(id+"F1.opExtrude","CAP_EDGE",EDGE,{"disambiguationData":[OSD([sQuery(id+"F0.wireOp",EDGE,"E34.MirrorC")])],"isStart":false});
            var Q108;
            Q108=makeQuery(id+"F1.opExtrude","CAP_EDGE",EDGE,{"disambiguationData":[OSD([sQuery(id+"F0.wireOp",EDGE,"E22")])],"isStart":true});
            var Q109;
            Q109=makeQuery(id+"F1.opExtrude","SWEPT_EDGE",EDGE,{"disambiguationData":[OSD([sQuery(id+"F0.wireOp",EDGE,"E39.2.12"),sQuery(id+"F0.wireOp",EDGE,"E39.2.7")])]});
            var Q110;
            Q110=makeQuery(id+"F1.opExtrude","CAP_EDGE",EDGE,{"disambiguationData":[OSD([sQuery(id+"F0.wireOp",EDGE,"E31")])],"isStart":false});
            var Q111;
            Q111=makeQuery(id+"F1.opExtrude","CAP_EDGE",EDGE,{"disambiguationData":[OSD([sQuery(id+"F0.wireOp",EDGE,"E39.2.4")])],"isStart":false});
            var Q112;
            Q112=makeQuery(id+"F1.opExtrude","CAP_EDGE",EDGE,{"disambiguationData":[OSD([sQuery(id+"F0.wireOp",EDGE,"E39.2.9")])],"isStart":false});
            var Q113;
            Q113=makeQuery(id+"F1.opExtrude","SWEPT_EDGE",EDGE,{"disambiguationData":[OSD([sQuery(id+"F0.wireOp",EDGE,"E39.2.7"),sQuery(id+"F0.wireOp",EDGE,"E39.2.6")])]});
            var Q114;
            Q114=makeQuery(id+"F1.opExtrude","CAP_EDGE",EDGE,{"disambiguationData":[OSD([sQuery(id+"F0.wireOp",EDGE,"E43.1.1")])],"isStart":false});
            var Q115;
            {var subQ0=sQuery(id+"F0.wireOp",EDGE,"E39.1.7");Q115=makeQuery(id+"F1.opExtrude","CAP_EDGE",EDGE,{"disambiguationData":[OSD([subQ0]),TDD([makeQuery(id+"F0.imprint","IMPRINT",EDGE,{"disambiguationData":[TD([[makeQuery(id+"F0.imprint","INTERSECT",VERTEX,{"derivedFrom":[sQuery(id+"F0.wireOp",EDGE,"E39.1.12"),subQ0]}),-1.0]])],"derivedFrom":subQ0})])],"isStart":false});}
            var Q116;
            Q116=makeQuery(id+"F1.opExtrude","CAP_EDGE",EDGE,{"disambiguationData":[OSD([sQuery(id+"F0.wireOp",EDGE,"E39.1.3")])],"isStart":false});
            var Q117;
            Q117=makeQuery(id+"F1.opExtrude","SWEPT_EDGE",EDGE,{"disambiguationData":[OSD([sQuery(id+"F0.wireOp",EDGE,"E39.1.8"),sQuery(id+"F0.wireOp",EDGE,"E39.1.9"),sQuery(id+"F0.wireOp",EDGE,"E39.1.10")])]});
            var Q118;
            Q118=makeQuery(id+"F1.opExtrude","CAP_EDGE",EDGE,{"disambiguationData":[OSD([sQuery(id+"F0.wireOp",EDGE,"E34.MirrorC")])],"isStart":true});
            var Q119;
            Q119=makeQuery(id+"F1.opExtrude","CAP_EDGE",EDGE,{"disambiguationData":[OSD([sQuery(id+"F0.wireOp",EDGE,"E32")])],"isStart":false});
            var Q120;
            Q120=makeQuery(id+"F1.opExtrude","CAP_EDGE",EDGE,{"disambiguationData":[OSD([sQuery(id+"F0.wireOp",EDGE,"E39.1.0")])],"isStart":false});
            var Q121;
            Q121=makeQuery(id+"F1.opExtrude","CAP_EDGE",EDGE,{"disambiguationData":[OSD([sQuery(id+"F0.wireOp",EDGE,"E20")])],"isStart":true});
            var Q122;
            Q122=makeQuery(id+"F1.opExtrude","CAP_EDGE",EDGE,{"disambiguationData":[OSD([sQuery(id+"F0.wireOp",EDGE,"E40.2.2")])],"isStart":true});
            var Q123;
            Q123=makeQuery(id+"F1.opExtrude","CAP_EDGE",EDGE,{"disambiguationData":[OSD([sQuery(id+"F0.wireOp",EDGE,"E39.2.11")])],"isStart":false});
            var Q124;
            Q124=makeQuery(id+"F1.opExtrude","CAP_EDGE",EDGE,{"disambiguationData":[OSD([sQuery(id+"F0.wireOp",EDGE,"E40.2.1")])],"isStart":false});
            var Q125;
            Q125=makeQuery(id+"F1.opExtrude","CAP_EDGE",EDGE,{"disambiguationData":[OSD([sQuery(id+"F0.wireOp",EDGE,"E33.MirrorC")])],"isStart":false});
            var Q126;
            Q126=makeQuery(id+"F1.opExtrude","CAP_EDGE",EDGE,{"disambiguationData":[OSD([sQuery(id+"F0.wireOp",EDGE,"E40.2.7")])],"isStart":false});
            var Q127;
            Q127=makeQuery(id+"F1.opExtrude","SWEPT_EDGE",EDGE,{"disambiguationData":[OSD([sQuery(id+"F0.wireOp",EDGE,"E40.2.0"),sQuery(id+"F0.wireOp",EDGE,"E43.2.1")])]});
            var Q128;
            Q128=makeQuery(id+"F1.opExtrude","SWEPT_EDGE",EDGE,{"disambiguationData":[OSD([sQuery(id+"F0.wireOp",EDGE,"E39.2.10"),sQuery(id+"F0.wireOp",EDGE,"E42.1.0")])]});
            var Q129;
            {var subQ0=sQuery(id+"F0.wireOp",EDGE,"E39.2.2");Q129=makeQuery(id+"F1.opExtrude","CAP_EDGE",EDGE,{"disambiguationData":[OSD([subQ0]),TDD([makeQuery(id+"F0.imprint","IMPRINT",EDGE,{"disambiguationData":[TD([[makeQuery(id+"F0.imprint","INTERSECT",VERTEX,{"derivedFrom":[subQ0,sQuery(id+"F0.wireOp",EDGE,"E39.2.5")]}),1.0]])],"derivedFrom":subQ0})])],"isStart":false});}
            var Q130;
            Q130=makeQuery(id+"F1.opExtrude","SWEPT_EDGE",EDGE,{"disambiguationData":[OSD([sQuery(id+"F0.wireOp",EDGE,"E39.1.0"),sQuery(id+"F0.wireOp",EDGE,"E39.1.1"),sQuery(id+"F0.wireOp",EDGE,"E39.1.3")])]});
            var Q131;
            Q131=makeQuery(id+"F1.opExtrude","CAP_EDGE",EDGE,{"disambiguationData":[OSD([sQuery(id+"F0.wireOp",EDGE,"E43.1.1")])],"isStart":true});
            var Q132;
            Q132=makeQuery(id+"F1.opExtrude","CAP_EDGE",EDGE,{"disambiguationData":[OSD([sQuery(id+"F0.wireOp",EDGE,"E40.2.10")])],"isStart":true});
            var Q133;
            Q133=makeQuery(id+"F1.opExtrude","SWEPT_EDGE",EDGE,{"disambiguationData":[OSD([sQuery(id+"F0.wireOp",EDGE,"E39.2.13"),sQuery(id+"F0.wireOp",EDGE,"E43.2.1")])]});
            var Q134;
            {var subQ0=sQuery(id+"F0.wireOp",EDGE,"E39.1.7");Q134=makeQuery(id+"F1.opExtrude","CAP_EDGE",EDGE,{"disambiguationData":[OSD([subQ0]),TDD([makeQuery(id+"F0.imprint","IMPRINT",EDGE,{"disambiguationData":[TD([[makeQuery(id+"F0.imprint","INTERSECT",VERTEX,{"derivedFrom":[subQ0,sQuery(id+"F0.wireOp",EDGE,"E39.1.5")]}),-1.0]])],"derivedFrom":subQ0})])],"isStart":false});}
            var Q135;
            Q135=makeQuery(id+"F1.opExtrude","CAP_EDGE",EDGE,{"disambiguationData":[OSD([sQuery(id+"F0.wireOp",EDGE,"E20")])],"isStart":false});
            var Q136;
            Q136=makeQuery(id+"F1.opExtrude","SWEPT_EDGE",EDGE,{"disambiguationData":[OSD([sQuery(id+"F0.wireOp",EDGE,"E39.1.3"),sQuery(id+"F0.wireOp",EDGE,"E42.1.0")])]});
            var Q137;
            Q137=makeQuery(id+"F1.opExtrude","CAP_EDGE",EDGE,{"disambiguationData":[OSD([sQuery(id+"F0.wireOp",EDGE,"E21")])],"isStart":false});
            var Q138;
            Q138=makeQuery(id+"F1.opExtrude","SWEPT_FACE",FACE,{"disambiguationData":[OSD([sQuery(id+"F0.wireOp",EDGE,"E36")])]});
            var Q139;
            {var subQ0=sQuery(id+"F0.wireOp",EDGE,"E39.2.2");Q139=makeQuery(id+"F1.opExtrude","CAP_EDGE",EDGE,{"disambiguationData":[OSD([subQ0]),TDD([makeQuery(id+"F0.imprint","IMPRINT",EDGE,{"disambiguationData":[TD([[makeQuery(id+"F0.imprint","INTERSECT",VERTEX,{"derivedFrom":[sQuery(id+"F0.wireOp",EDGE,"E40.2.2"),subQ0]}),1.0]])],"derivedFrom":subQ0})])],"isStart":false});}
            var Q140;
            Q140=makeQuery(id+"F1.opExtrude","SWEPT_EDGE",EDGE,{"disambiguationData":[OSD([sQuery(id+"F0.wireOp",EDGE,"E39.2.7"),sQuery(id+"F0.wireOp",EDGE,"E39.2.5")])]});
            var Q141;
            Q141=makeQuery(id+"F1.opExtrude","SWEPT_EDGE",EDGE,{"disambiguationData":[OSD([sQuery(id+"F0.wireOp",EDGE,"E39.2.8"),sQuery(id+"F0.wireOp",EDGE,"E39.2.9"),sQuery(id+"F0.wireOp",EDGE,"E39.2.7")])]});
            var Q142;
            Q142=makeQuery(id+"F1.opExtrude","CAP_EDGE",EDGE,{"disambiguationData":[OSD([sQuery(id+"F0.wireOp",EDGE,"E39.1.10")])],"isStart":true});
            var Q143;
            Q143=makeQuery(id+"F1.opExtrude","CAP_EDGE",EDGE,{"disambiguationData":[OSD([sQuery(id+"F0.wireOp",EDGE,"E40.2.10")])],"isStart":false});
            var Q144;
            Q144=makeQuery(id+"F1.opExtrude","SWEPT_EDGE",EDGE,{"disambiguationData":[OSD([sQuery(id+"F0.wireOp",EDGE,"E40.1.1"),sQuery(id+"F0.wireOp",EDGE,"E40.1.2")])]});
            var Q145;
            Q145=makeQuery(id+"F1.opExtrude","CAP_EDGE",EDGE,{"disambiguationData":[OSD([sQuery(id+"F0.wireOp",EDGE,"E40.2.7")])],"isStart":true});
            var Q146;
            Q146=makeQuery(id+"F1.opExtrude","CAP_EDGE",EDGE,{"disambiguationData":[OSD([sQuery(id+"F0.wireOp",EDGE,"E39.2.4")])],"isStart":true});
            var Q147;
            Q147=makeQuery(id+"F1.opExtrude","CAP_EDGE",EDGE,{"disambiguationData":[OSD([sQuery(id+"F0.wireOp",EDGE,"E39.2.13")])],"isStart":true});
            var Q148;
            Q148=makeQuery(id+"F1.opExtrude","SWEPT_EDGE",EDGE,{"disambiguationData":[OSD([sQuery(id+"F0.wireOp",EDGE,"E26"),sQuery(id+"F0.wireOp",EDGE,"E42.2.0")])]});
            var Q149;
            Q149=makeQuery(id+"F1.opExtrude","SWEPT_FACE",FACE,{"disambiguationData":[OSD([sQuery(id+"F0.wireOp",EDGE,"E39.2.12")])]});
            var Q150;
            {var subQ0=sQuery(id+"F0.wireOp",EDGE,"E39.2.2");Q150=makeQuery(id+"F1.opExtrude","CAP_EDGE",EDGE,{"disambiguationData":[OSD([subQ0]),TDD([makeQuery(id+"F0.imprint","IMPRINT",EDGE,{"disambiguationData":[TD([[makeQuery(id+"F0.imprint","INTERSECT",VERTEX,{"derivedFrom":[subQ0,sQuery(id+"F0.wireOp",EDGE,"E39.2.5")]}),1.0]])],"derivedFrom":subQ0})])],"isStart":true});}
            var Q151;
            Q151=makeQuery(id+"F1.opExtrude","CAP_EDGE",EDGE,{"disambiguationData":[OSD([sQuery(id+"F0.wireOp",EDGE,"E39.2.11")])],"isStart":true});
            var Q152;
            Q152=makeQuery(id+"F1.opExtrude","CAP_EDGE",EDGE,{"disambiguationData":[OSD([sQuery(id+"F0.wireOp",EDGE,"E43.2.1")])],"isStart":true});
            var Q153;
            Q153=makeQuery(id+"F1.opExtrude","SWEPT_EDGE",EDGE,{"disambiguationData":[OSD([sQuery(id+"F0.wireOp",EDGE,"E25"),sQuery(id+"F0.wireOp",EDGE,"E26"),sQuery(id+"F0.wireOp",EDGE,"E38.MirrorCS")])]});
            var Q154;
            Q154=makeQuery(id+"F1.opExtrude","SWEPT_EDGE",EDGE,{"disambiguationData":[OSD([sQuery(id+"F0.wireOp",EDGE,"E24"),sQuery(id+"F0.wireOp",EDGE,"E25"),sQuery(id+"F0.wireOp",EDGE,"E38.MirrorCS")])]});
            var Q155;
            Q155=makeQuery(id+"F1.opExtrude","CAP_EDGE",EDGE,{"disambiguationData":[OSD([sQuery(id+"F0.wireOp",EDGE,"E32")])],"isStart":true});
            var Q156;
            Q156=makeQuery(id+"F1.opExtrude","CAP_EDGE",EDGE,{"disambiguationData":[OSD([sQuery(id+"F0.wireOp",EDGE,"E40.2.1")])],"isStart":true});
            var Q157;
            {var subQ0=sQuery(id+"F0.wireOp",EDGE,"E39.1.7");Q157=makeQuery(id+"F1.opExtrude","CAP_EDGE",EDGE,{"disambiguationData":[OSD([subQ0]),TDD([makeQuery(id+"F0.imprint","IMPRINT",EDGE,{"disambiguationData":[TD([[makeQuery(id+"F0.imprint","INTERSECT",VERTEX,{"derivedFrom":[sQuery(id+"F0.wireOp",EDGE,"E39.1.12"),subQ0]}),-1.0]])],"derivedFrom":subQ0})])],"isStart":true});}
            var Q158;
            Q158=makeQuery(id+"F1.opExtrude","CAP_EDGE",EDGE,{"disambiguationData":[OSD([sQuery(id+"F0.wireOp",EDGE,"E40.2.0")])],"isStart":true});
            var Q159;
            Q159=makeQuery(id+"F1.opExtrude","CAP_EDGE",EDGE,{"disambiguationData":[OSD([sQuery(id+"F0.wireOp",EDGE,"E39.2.9")])],"isStart":true});
            var Q160;
            Q160=makeQuery(id+"F1.opExtrude","CAP_EDGE",EDGE,{"disambiguationData":[OSD([sQuery(id+"F0.wireOp",EDGE,"E39.1.0")])],"isStart":true});
            var Q161;
            Q161=makeQuery(id+"F1.opExtrude","CAP_EDGE",EDGE,{"disambiguationData":[OSD([sQuery(id+"F0.wireOp",EDGE,"E31")])],"isStart":true});
            var Q162;
            {var subQ0=sQuery(id+"F0.wireOp",EDGE,"E39.1.7");Q162=makeQuery(id+"F1.opExtrude","CAP_EDGE",EDGE,{"disambiguationData":[OSD([subQ0]),TDD([makeQuery(id+"F0.imprint","IMPRINT",EDGE,{"disambiguationData":[TD([[makeQuery(id+"F0.imprint","INTERSECT",VERTEX,{"derivedFrom":[subQ0,sQuery(id+"F0.wireOp",EDGE,"E39.1.5")]}),-1.0]])],"derivedFrom":subQ0})])],"isStart":true});}
            var Q163;
            Q163=makeQuery(id+"F1.opExtrude","CAP_EDGE",EDGE,{"disambiguationData":[OSD([sQuery(id+"F0.wireOp",EDGE,"E19")])],"isStart":true});
            var Q164;
            Q164=makeQuery(id+"F1.opExtrude","SWEPT_EDGE",EDGE,{"disambiguationData":[OSD([sQuery(id+"F0.wireOp",EDGE,"E39.2.8"),sQuery(id+"F0.wireOp",EDGE,"E39.2.9"),sQuery(id+"F0.wireOp",EDGE,"E39.2.10")])]});
            var Q165;
            Q165=makeQuery(id+"F1.opExtrude","SWEPT_EDGE",EDGE,{"disambiguationData":[OSD([sQuery(id+"F0.wireOp",EDGE,"E39.2.2"),sQuery(id+"F0.wireOp",EDGE,"E39.2.6")])]});
            var Q166;
            Q166=makeQuery(id+"F1.opExtrude","CAP_EDGE",EDGE,{"disambiguationData":[OSD([sQuery(id+"F0.wireOp",EDGE,"E43.2.1")])],"isStart":false});
            var Q167;
            Q167=makeQuery(id+"F1.opExtrude","CAP_EDGE",EDGE,{"disambiguationData":[OSD([sQuery(id+"F0.wireOp",EDGE,"E39.2.12")])],"isStart":true});
            var Q168;
            Q168=makeQuery(id+"F1.opExtrude","CAP_EDGE",EDGE,{"disambiguationData":[OSD([sQuery(id+"F0.wireOp",EDGE,"E39.1.6")])],"isStart":true});
            var Q169;
            Q169=makeQuery(id+"F1.opExtrude","CAP_EDGE",EDGE,{"disambiguationData":[OSD([sQuery(id+"F0.wireOp",EDGE,"E33.MirrorC")])],"isStart":true});
            var Q170;
            Q170=makeQuery(id+"F1.opExtrude","CAP_EDGE",EDGE,{"disambiguationData":[OSD([sQuery(id+"F0.wireOp",EDGE,"E21")])],"isStart":true});
            var Q171;
            Q171=makeQuery(id+"F1.opExtrude","SWEPT_EDGE",EDGE,{"disambiguationData":[OSD([sQuery(id+"F0.wireOp",EDGE,"E39.2.12"),sQuery(id+"F0.wireOp",EDGE,"E39.2.13")])]});
            var Q172;
            Q172=makeQuery(id+"F1.opExtrude","SWEPT_EDGE",EDGE,{"disambiguationData":[OSD([sQuery(id+"F0.wireOp",EDGE,"E39.1.0"),sQuery(id+"F0.wireOp",EDGE,"E39.1.1"),sQuery(id+"F0.wireOp",EDGE,"E39.1.2")])]});
            var Q173;
            Q173=makeQuery(id+"F1.opExtrude","SWEPT_EDGE",EDGE,{"disambiguationData":[OSD([sQuery(id+"F0.wireOp",EDGE,"E22"),sQuery(id+"F0.wireOp",EDGE,"E23")])]});
            var Q174;
            Q174=makeQuery(id+"F1.opExtrude","SWEPT_EDGE",EDGE,{"disambiguationData":[OSD([sQuery(id+"F0.wireOp",EDGE,"E21"),sQuery(id+"F0.wireOp",EDGE,"E22")])]});
            var Q175;
            Q175=makeQuery(id+"F1.opExtrude","SWEPT_EDGE",EDGE,{"disambiguationData":[OSD([sQuery(id+"F0.wireOp",EDGE,"E20"),sQuery(id+"F0.wireOp",EDGE,"E21")])]});
            var Q176;
            Q176=makeQuery(id+"F1.opExtrude","SWEPT_EDGE",EDGE,{"disambiguationData":[OSD([sQuery(id+"F0.wireOp",EDGE,"E19"),sQuery(id+"F0.wireOp",EDGE,"E20")])]});
            var Q177;
            Q177=makeQuery(id+"F1.opExtrude","SWEPT_EDGE",EDGE,{"disambiguationData":[OSD([sQuery(id+"F0.wireOp",EDGE,"E18"),sQuery(id+"F0.wireOp",EDGE,"E19")])]});
            var Q178;
            Q178=makeQuery(id+"F1.opExtrude","SWEPT_EDGE",EDGE,{"disambiguationData":[OSD([sQuery(id+"F0.wireOp",EDGE,"E39.1.8"),sQuery(id+"F0.wireOp",EDGE,"E39.1.9"),sQuery(id+"F0.wireOp",EDGE,"E39.1.7")])]});
            var Q179;
            Q179=makeQuery(id+"F1.opExtrude","CAP_EDGE",EDGE,{"disambiguationData":[OSD([sQuery(id+"F0.wireOp",EDGE,"E15")])],"isStart":true});
            var Q180;
            Q180=makeQuery(id+"F1.opExtrude","SWEPT_EDGE",EDGE,{"disambiguationData":[OSD([sQuery(id+"F0.wireOp",EDGE,"E40.1.2"),sQuery(id+"F0.wireOp",EDGE,"E39.1.2")])]});
            var Q181;
            Q181=makeQuery(id+"F1.opExtrude","CAP_EDGE",EDGE,{"disambiguationData":[OSD([sQuery(id+"F0.wireOp",EDGE,"E39.1.12")])],"isStart":true});
            var Q182;
            Q182=makeQuery(id+"F1.opExtrude","CAP_EDGE",EDGE,{"disambiguationData":[OSD([sQuery(id+"F0.wireOp",EDGE,"E40.1.7")])],"isStart":true});
            var Q183;
            Q183=makeQuery(id+"F1.opExtrude","CAP_EDGE",EDGE,{"disambiguationData":[OSD([sQuery(id+"F0.wireOp",EDGE,"E40.1.1")])],"isStart":true});
            var Q184;
            {var subQ0=sQuery(id+"F0.wireOp",EDGE,"E39.2.7");Q184=makeQuery(id+"F1.opExtrude","CAP_EDGE",EDGE,{"disambiguationData":[OSD([subQ0]),TDD([makeQuery(id+"F0.imprint","IMPRINT",EDGE,{"disambiguationData":[TD([[makeQuery(id+"F0.imprint","INTERSECT",VERTEX,{"derivedFrom":[sQuery(id+"F0.wireOp",EDGE,"E39.2.12"),subQ0]}),-1.0]])],"derivedFrom":subQ0})])],"isStart":true});}
            var Q185;
            Q185=makeQuery(id+"F1.opExtrude","SWEPT_EDGE",EDGE,{"disambiguationData":[OSD([sQuery(id+"F0.wireOp",EDGE,"E39.1.10"),sQuery(id+"F0.wireOp",EDGE,"E41")])]});
            var Q186;
            Q186=makeQuery(id+"F1.opExtrude","SWEPT_EDGE",EDGE,{"disambiguationData":[OSD([sQuery(id+"F0.wireOp",EDGE,"E39.1.2"),sQuery(id+"F0.wireOp",EDGE,"E39.1.6")])]});
            var Q187;
            Q187=makeQuery(id+"F1.opExtrude","CAP_EDGE",EDGE,{"disambiguationData":[OSD([sQuery(id+"F0.wireOp",EDGE,"E15")])],"isStart":false});
            var Q188;
            Q188=makeQuery(id+"F1.opExtrude","CAP_EDGE",EDGE,{"disambiguationData":[OSD([sQuery(id+"F0.wireOp",EDGE,"E39.1.12")])],"isStart":false});
            var Q189;
            Q189=makeQuery(id+"F1.opExtrude","CAP_EDGE",EDGE,{"disambiguationData":[OSD([sQuery(id+"F0.wireOp",EDGE,"E40.1.1")])],"isStart":false});
            var Q190;
            Q190=makeQuery(id+"F1.opExtrude","CAP_EDGE",EDGE,{"disambiguationData":[OSD([sQuery(id+"F0.wireOp",EDGE,"E40.1.7")])],"isStart":false});
            var Q191;
            {var subQ0=sQuery(id+"F0.wireOp",EDGE,"E39.2.7");Q191=makeQuery(id+"F1.opExtrude","CAP_EDGE",EDGE,{"disambiguationData":[OSD([subQ0]),TDD([makeQuery(id+"F0.imprint","IMPRINT",EDGE,{"disambiguationData":[TD([[makeQuery(id+"F0.imprint","INTERSECT",VERTEX,{"derivedFrom":[sQuery(id+"F0.wireOp",EDGE,"E39.2.12"),subQ0]}),-1.0]])],"derivedFrom":subQ0})])],"isStart":false});}
            var Q192;
            {var subQ0=sQuery(id+"F0.wireOp",EDGE,"E17");Q192=makeQuery(id+"F1.opExtrude","CAP_EDGE",EDGE,{"disambiguationData":[OSD([subQ0]),TDD([makeQuery(id+"F0.imprint","IMPRINT",EDGE,{"disambiguationData":[TD([[makeQuery(id+"F0.imprint","INTERSECT",VERTEX,{"derivedFrom":[subQ0,sQuery(id+"F0.wireOp",EDGE,"E36")]}),1.0]])],"derivedFrom":subQ0})])],"isStart":true});}
            var Q193;
            Q193=makeQuery(id+"F1.opExtrude","SWEPT_EDGE",EDGE,{"disambiguationData":[OSD([sQuery(id+"F0.wireOp",EDGE,"E39.1.7"),sQuery(id+"F0.wireOp",EDGE,"E39.1.6")])]});
            var Q194;
            {var subQ0=sQuery(id+"F0.wireOp",EDGE,"E24");Q194=makeQuery(id+"F1.opExtrude","CAP_EDGE",EDGE,{"disambiguationData":[OSD([subQ0]),TDD([makeQuery(id+"F0.imprint","IMPRINT",EDGE,{"disambiguationData":[TD([[makeQuery(id+"F0.imprint","INTERSECT",VERTEX,{"derivedFrom":[sQuery(id+"F0.wireOp",EDGE,"E23"),subQ0]}),-1.0]])],"derivedFrom":subQ0})])],"isStart":true});}
            var Q195;
            Q195=makeQuery(id+"F1.opExtrude","CAP_EDGE",EDGE,{"disambiguationData":[OSD([sQuery(id+"F0.wireOp",EDGE,"E36")])],"isStart":true});
            var Q196;
            Q196=makeQuery(id+"F1.opExtrude","CAP_EDGE",EDGE,{"disambiguationData":[OSD([sQuery(id+"F0.wireOp",EDGE,"E39.1.13")])],"isStart":true});
            var Q197;
            Q197=makeQuery(id+"F1.opExtrude","CAP_EDGE",EDGE,{"disambiguationData":[OSD([sQuery(id+"F0.wireOp",EDGE,"E39.1.4")])],"isStart":true});
            var Q198;
            Q198=makeQuery(id+"F1.opExtrude","CAP_EDGE",EDGE,{"disambiguationData":[OSD([sQuery(id+"F0.wireOp",EDGE,"E40.1.2")])],"isStart":true});
            var Q199;
            {var subQ0=sQuery(id+"F0.wireOp",EDGE,"E39.2.7");Q199=makeQuery(id+"F1.opExtrude","CAP_EDGE",EDGE,{"disambiguationData":[OSD([subQ0]),TDD([makeQuery(id+"F0.imprint","IMPRINT",EDGE,{"disambiguationData":[TD([[makeQuery(id+"F0.imprint","INTERSECT",VERTEX,{"derivedFrom":[subQ0,sQuery(id+"F0.wireOp",EDGE,"E39.2.5")]}),-1.0]])],"derivedFrom":subQ0})])],"isStart":true});}
            var Q200;
            {var subQ0=sQuery(id+"F0.wireOp",EDGE,"E17");Q200=makeQuery(id+"F1.opExtrude","CAP_EDGE",EDGE,{"disambiguationData":[OSD([subQ0]),TDD([makeQuery(id+"F0.imprint","IMPRINT",EDGE,{"disambiguationData":[TD([[makeQuery(id+"F0.imprint","INTERSECT",VERTEX,{"derivedFrom":[subQ0,sQuery(id+"F0.wireOp",EDGE,"E36")]}),1.0]])],"derivedFrom":subQ0})])],"isStart":false});}
            var Q201;
            Q201=makeQuery(id+"F1.opExtrude","SWEPT_EDGE",EDGE,{"disambiguationData":[OSD([sQuery(id+"F0.wireOp",EDGE,"E39.1.12"),sQuery(id+"F0.wireOp",EDGE,"E39.1.13")])]});
            var Q202;
            {var subQ0=sQuery(id+"F0.wireOp",EDGE,"E24");Q202=makeQuery(id+"F1.opExtrude","CAP_EDGE",EDGE,{"disambiguationData":[OSD([subQ0]),TDD([makeQuery(id+"F0.imprint","IMPRINT",EDGE,{"disambiguationData":[TD([[makeQuery(id+"F0.imprint","INTERSECT",VERTEX,{"derivedFrom":[sQuery(id+"F0.wireOp",EDGE,"E23"),subQ0]}),-1.0]])],"derivedFrom":subQ0})])],"isStart":false});}
            var Q203;
            Q203=makeQuery(id+"F1.opExtrude","SWEPT_EDGE",EDGE,{"disambiguationData":[OSD([sQuery(id+"F0.wireOp",EDGE,"E16"),sQuery(id+"F0.wireOp",EDGE,"E17"),sQuery(id+"F0.wireOp",EDGE,"E37")])]});
            var Q204;
            Q204=makeQuery(id+"F1.opExtrude","CAP_EDGE",EDGE,{"disambiguationData":[OSD([sQuery(id+"F0.wireOp",EDGE,"E39.1.13")])],"isStart":false});
            var Q205;
            Q205=makeQuery(id+"F1.opExtrude","CAP_EDGE",EDGE,{"disambiguationData":[OSD([sQuery(id+"F0.wireOp",EDGE,"E40.1.2")])],"isStart":false});
            var Q206;
            Q206=makeQuery(id+"F1.opExtrude","CAP_EDGE",EDGE,{"disambiguationData":[OSD([sQuery(id+"F0.wireOp",EDGE,"E39.1.4")])],"isStart":false});
            var Q207;
            {var subQ0=sQuery(id+"F0.wireOp",EDGE,"E39.2.7");Q207=makeQuery(id+"F1.opExtrude","CAP_EDGE",EDGE,{"disambiguationData":[OSD([subQ0]),TDD([makeQuery(id+"F0.imprint","IMPRINT",EDGE,{"disambiguationData":[TD([[makeQuery(id+"F0.imprint","INTERSECT",VERTEX,{"derivedFrom":[subQ0,sQuery(id+"F0.wireOp",EDGE,"E39.2.5")]}),-1.0]])],"derivedFrom":subQ0})])],"isStart":false});}
            var Q208;
            Q208=makeQuery(id+"F1.opExtrude","SWEPT_EDGE",EDGE,{"disambiguationData":[OSD([sQuery(id+"F0.wireOp",EDGE,"E15"),sQuery(id+"F0.wireOp",EDGE,"E16"),sQuery(id+"F0.wireOp",EDGE,"E37")])]});
            var Q209;
            Q209=makeQuery(id+"F1.opExtrude","SWEPT_EDGE",EDGE,{"disambiguationData":[OSD([sQuery(id+"F0.wireOp",EDGE,"E15"),sQuery(id+"F0.wireOp",EDGE,"E41")])]});
            var Q210;
            Q210=makeQuery(id+"F1.opExtrude","SWEPT_EDGE",EDGE,{"disambiguationData":[OSD([sQuery(id+"F0.wireOp",EDGE,"E24"),sQuery(id+"F0.wireOp",EDGE,"E35")])]});
            var Q211;
            Q211=makeQuery(id+"F1.opExtrude","SWEPT_EDGE",EDGE,{"disambiguationData":[OSD([sQuery(id+"F0.wireOp",EDGE,"E17"),sQuery(id+"F0.wireOp",EDGE,"E35")])]});
            var Q212;
            Q212=makeQuery(id+"F1.opExtrude","SWEPT_EDGE",EDGE,{"disambiguationData":[OSD([sQuery(id+"F0.wireOp",EDGE,"E39.1.2"),sQuery(id+"F0.wireOp",EDGE,"E39.1.5")])]});
            var Q213;
            {var subQ0=sQuery(id+"F0.wireOp",EDGE,"E17");Q213=makeQuery(id+"F1.opExtrude","CAP_EDGE",EDGE,{"disambiguationData":[OSD([subQ0]),TDD([makeQuery(id+"F0.imprint","IMPRINT",EDGE,{"disambiguationData":[TD([[makeQuery(id+"F0.imprint","INTERSECT",VERTEX,{"derivedFrom":[subQ0,sQuery(id+"F0.wireOp",EDGE,"E18")]}),1.0]])],"derivedFrom":subQ0})])],"isStart":true});}
            var Q214;
            {var subQ0=sQuery(id+"F0.wireOp",EDGE,"E24");Q214=makeQuery(id+"F1.opExtrude","CAP_EDGE",EDGE,{"disambiguationData":[OSD([subQ0]),TDD([makeQuery(id+"F0.imprint","IMPRINT",EDGE,{"disambiguationData":[TD([[makeQuery(id+"F0.imprint","INTERSECT",VERTEX,{"derivedFrom":[subQ0,sQuery(id+"F0.wireOp",EDGE,"E36")]}),-1.0]])],"derivedFrom":subQ0})])],"isStart":true});}
            var Q215;
            Q215=makeQuery(id+"F1.opExtrude","CAP_EDGE",EDGE,{"disambiguationData":[OSD([sQuery(id+"F0.wireOp",EDGE,"E37")])],"isStart":true});
            var Q216;
            Q216=makeQuery(id+"F1.opExtrude","CAP_EDGE",EDGE,{"disambiguationData":[OSD([sQuery(id+"F0.wireOp",EDGE,"E39.2.0")])],"isStart":true});
            var Q217;
            {var subQ0=sQuery(id+"F0.wireOp",EDGE,"E39.1.2");Q217=makeQuery(id+"F1.opExtrude","CAP_EDGE",EDGE,{"disambiguationData":[OSD([subQ0]),TDD([makeQuery(id+"F0.imprint","IMPRINT",EDGE,{"disambiguationData":[TD([[makeQuery(id+"F0.imprint","INTERSECT",VERTEX,{"derivedFrom":[subQ0,sQuery(id+"F0.wireOp",EDGE,"E39.1.5")]}),1.0]])],"derivedFrom":subQ0})])],"isStart":true});}
            var Q218;
            Q218=makeQuery(id+"F1.opExtrude","CAP_EDGE",EDGE,{"disambiguationData":[OSD([sQuery(id+"F0.wireOp",EDGE,"E39.1.11")])],"isStart":true});
            var Q219;
            Q219=makeQuery(id+"F1.opExtrude","CAP_EDGE",EDGE,{"disambiguationData":[OSD([sQuery(id+"F0.wireOp",EDGE,"E39.2.6")])],"isStart":true});
            var Q220;
            Q220=makeQuery(id+"F1.opExtrude","CAP_EDGE",EDGE,{"disambiguationData":[OSD([sQuery(id+"F0.wireOp",EDGE,"E42.2.0")])],"isStart":true});
            var Q221;
            Q221=makeQuery(id+"F1.opExtrude","SWEPT_EDGE",EDGE,{"disambiguationData":[OSD([sQuery(id+"F0.wireOp",EDGE,"E39.2.0"),sQuery(id+"F0.wireOp",EDGE,"E39.2.1"),sQuery(id+"F0.wireOp",EDGE,"E39.2.2")])]});
            var Q222;
            {var subQ0=sQuery(id+"F0.wireOp",EDGE,"E17");Q222=makeQuery(id+"F1.opExtrude","CAP_EDGE",EDGE,{"disambiguationData":[OSD([subQ0]),TDD([makeQuery(id+"F0.imprint","IMPRINT",EDGE,{"disambiguationData":[TD([[makeQuery(id+"F0.imprint","INTERSECT",VERTEX,{"derivedFrom":[subQ0,sQuery(id+"F0.wireOp",EDGE,"E18")]}),1.0]])],"derivedFrom":subQ0})])],"isStart":false});}
            var Q223;
            {var subQ0=sQuery(id+"F0.wireOp",EDGE,"E24");Q223=makeQuery(id+"F1.opExtrude","CAP_EDGE",EDGE,{"disambiguationData":[OSD([subQ0]),TDD([makeQuery(id+"F0.imprint","IMPRINT",EDGE,{"disambiguationData":[TD([[makeQuery(id+"F0.imprint","INTERSECT",VERTEX,{"derivedFrom":[subQ0,sQuery(id+"F0.wireOp",EDGE,"E36")]}),-1.0]])],"derivedFrom":subQ0})])],"isStart":false});}
            var Q224;
            Q224=makeQuery(id+"F1.opExtrude","CAP_EDGE",EDGE,{"disambiguationData":[OSD([sQuery(id+"F0.wireOp",EDGE,"E37")])],"isStart":false});
            var Q225;
            Q225=makeQuery(id+"F1.opExtrude","CAP_EDGE",EDGE,{"disambiguationData":[OSD([sQuery(id+"F0.wireOp",EDGE,"E39.2.0")])],"isStart":false});
            var Q226;
            Q226=makeQuery(id+"F1.opExtrude","CAP_EDGE",EDGE,{"disambiguationData":[OSD([sQuery(id+"F0.wireOp",EDGE,"E39.1.11")])],"isStart":false});
            var Q227;
            Q227=makeQuery(id+"F1.opExtrude","CAP_EDGE",EDGE,{"disambiguationData":[OSD([sQuery(id+"F0.wireOp",EDGE,"E39.2.6")])],"isStart":false});
            var Q228;
            Q228=makeQuery(id+"F1.opExtrude","SWEPT_EDGE",EDGE,{"disambiguationData":[OSD([sQuery(id+"F0.wireOp",EDGE,"E39.2.0"),sQuery(id+"F0.wireOp",EDGE,"E39.2.1"),sQuery(id+"F0.wireOp",EDGE,"E39.2.3")])]});
            var Q229;
            Q229=makeQuery(id+"F1.opExtrude","CAP_EDGE",EDGE,{"disambiguationData":[OSD([sQuery(id+"F0.wireOp",EDGE,"E18")])],"isStart":true});
            var Q230;
            Q230=makeQuery(id+"F1.opExtrude","CAP_EDGE",EDGE,{"disambiguationData":[OSD([sQuery(id+"F0.wireOp",EDGE,"E26")])],"isStart":true});
            var Q231;
            Q231=makeQuery(id+"F1.opExtrude","CAP_EDGE",EDGE,{"disambiguationData":[OSD([sQuery(id+"F0.wireOp",EDGE,"E38.MirrorCS")])],"isStart":true});
            var Q232;
            Q232=makeQuery(id+"F1.opExtrude","CAP_EDGE",EDGE,{"disambiguationData":[OSD([sQuery(id+"F0.wireOp",EDGE,"E39.2.3")])],"isStart":true});
            var Q233;
            {var subQ0=sQuery(id+"F0.wireOp",EDGE,"E39.1.2");Q233=makeQuery(id+"F1.opExtrude","CAP_EDGE",EDGE,{"disambiguationData":[OSD([subQ0]),TDD([makeQuery(id+"F0.imprint","IMPRINT",EDGE,{"disambiguationData":[TD([[makeQuery(id+"F0.imprint","INTERSECT",VERTEX,{"derivedFrom":[sQuery(id+"F0.wireOp",EDGE,"E40.1.2"),subQ0]}),1.0]])],"derivedFrom":subQ0})])],"isStart":true});}
            var Q234;
            Q234=makeQuery(id+"F1.opExtrude","CAP_EDGE",EDGE,{"disambiguationData":[OSD([sQuery(id+"F0.wireOp",EDGE,"E40.1.10")])],"isStart":true});
            var Q235;
            Q235=makeQuery(id+"F1.opExtrude","CAP_EDGE",EDGE,{"disambiguationData":[OSD([sQuery(id+"F0.wireOp",EDGE,"E39.2.5")])],"isStart":true});
            var Q236;
            Q236=makeQuery(id+"F1.opExtrude","CAP_EDGE",EDGE,{"disambiguationData":[OSD([sQuery(id+"F0.wireOp",EDGE,"E40.1.0")])],"isStart":true});
            var Q237;
            Q237=makeQuery(id+"F1.opExtrude","SWEPT_EDGE",EDGE,{"disambiguationData":[OSD([sQuery(id+"F0.wireOp",EDGE,"E39.2.3"),sQuery(id+"F0.wireOp",EDGE,"E42.2.0")])]});
            var Q238;
            Q238=makeQuery(id+"F1.opExtrude","CAP_EDGE",EDGE,{"disambiguationData":[OSD([sQuery(id+"F0.wireOp",EDGE,"E38.MirrorCS")])],"isStart":false});
            var Q239;
            {var subQ0=sQuery(id+"F0.wireOp",EDGE,"E39.1.2");Q239=makeQuery(id+"F1.opExtrude","CAP_EDGE",EDGE,{"disambiguationData":[OSD([subQ0]),TDD([makeQuery(id+"F0.imprint","IMPRINT",EDGE,{"disambiguationData":[TD([[makeQuery(id+"F0.imprint","INTERSECT",VERTEX,{"derivedFrom":[sQuery(id+"F0.wireOp",EDGE,"E40.1.2"),subQ0]}),1.0]])],"derivedFrom":subQ0})])],"isStart":false});}
            var Q240;
            Q240=makeQuery(id+"F1.opExtrude","CAP_EDGE",EDGE,{"disambiguationData":[OSD([sQuery(id+"F0.wireOp",EDGE,"E40.1.10")])],"isStart":false});
            var Q241;
            Q241=makeQuery(id+"F1.opExtrude","CAP_EDGE",EDGE,{"disambiguationData":[OSD([sQuery(id+"F0.wireOp",EDGE,"E39.2.5")])],"isStart":false});
            var Q242;
            Q242=makeQuery(id+"F1.opExtrude","CAP_EDGE",EDGE,{"disambiguationData":[OSD([sQuery(id+"F0.wireOp",EDGE,"E40.1.0")])],"isStart":false});
            var Q243;
            Q243=makeQuery(id+"F1.opExtrude","SWEPT_EDGE",EDGE,{"disambiguationData":[OSD([sQuery(id+"F0.wireOp",EDGE,"E17"),sQuery(id+"F0.wireOp",EDGE,"E36")])]});
            var Q244;
            Q244=makeQuery(id+"F1.opExtrude","SWEPT_EDGE",EDGE,{"disambiguationData":[OSD([sQuery(id+"F0.wireOp",EDGE,"E24"),sQuery(id+"F0.wireOp",EDGE,"E36")])]});
            fillet(context, id + "F2", {"entities" : qUnion([Q0, Q1, Q2, Q3, Q4, Q5, Q6, Q7, Q8, Q9, Q10, Q11, Q12, Q13, Q14, Q15, Q16, Q17, Q18, Q19, Q20, Q21, Q22, Q23, Q24, Q25, Q26, Q27, Q28, Q29, Q30, Q31, Q32, Q33, Q34, Q35, Q36, Q37, Q38, Q39, Q40, Q41, Q42, Q43, Q44, Q45, Q46, Q47, Q48, Q49, Q50, Q51, Q52, Q53, Q54, Q55, Q56, Q57, Q58, Q59, Q60, Q61, Q62, Q63, Q64, Q65, Q66, Q67, Q68, Q69, Q70, Q71, Q72, Q73, Q74, Q75, Q76, Q77, Q78, Q79, Q80, Q81, Q82, Q83, Q84, Q85, Q86, Q87, Q88, Q89, Q90, Q91, Q92, Q93, Q94, Q95, Q96, Q97, Q98, Q99, Q100, Q101, Q102, Q103, Q104, Q105, Q106, Q107, Q108, Q109, Q110, Q111, Q112, Q113, Q114, Q115, Q116, Q117, Q118, Q119, Q120, Q121, Q122, Q123, Q124, Q125, Q126, Q127, Q128, Q129, Q130, Q131, Q132, Q133, Q134, Q135, Q136, Q137, Q138, Q139, Q140, Q141, Q142, Q143, Q144, Q145, Q146, Q147, Q148, Q149, Q150, Q151, Q152, Q153, Q154, Q155, Q156, Q157, Q158, Q159, Q160, Q161, Q162, Q163, Q164, Q165, Q166, Q167, Q168, Q169, Q170, Q171, Q172, Q173, Q174, Q175, Q176, Q177, Q178, Q179, Q180, Q181, Q182, Q183, Q184, Q185, Q186, Q187, Q188, Q189, Q190, Q191, Q192, Q193, Q194, Q195, Q196, Q197, Q198, Q199, Q200, Q201, Q202, Q203, Q204, Q205, Q206, Q207, Q208, Q209, Q210, Q211, Q212, Q213, Q214, Q215, Q216, Q217, Q218, Q219, Q220, Q221, Q222, Q223, Q224, Q225, Q226, Q227, Q228, Q229, Q230, Q231, Q232, Q233, Q234, Q235, Q236, Q237, Q238, Q239, Q240, Q241, Q242, Q243, Q244]), "radius" : 0.5 * mm, "tangentPropagation" : true, "allowEdgeOverflow" : false});
        }
    });
